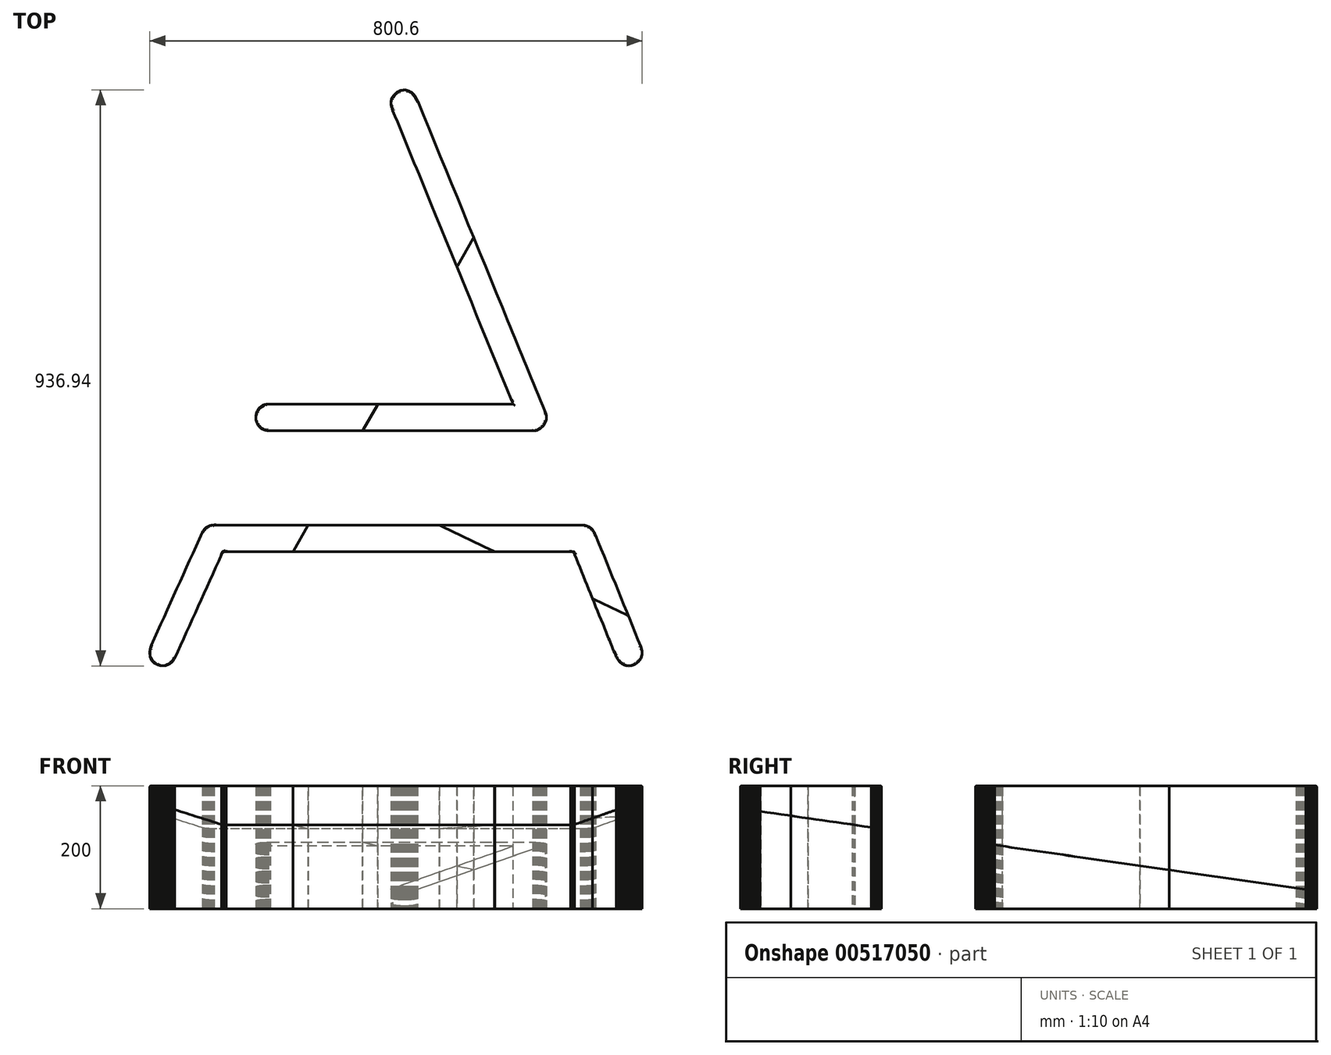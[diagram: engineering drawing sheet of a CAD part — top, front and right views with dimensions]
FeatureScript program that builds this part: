
annotation { "Feature Type Name" : "Feature", "Feature Type Description" : "" }
export const myFeature = defineFeature(function(context is Context, id is Id, definition is map)
    precondition{}
    {
        {
            var Q0;
            Q0=qCreatedBy(makeId("Top.planeOp"),FACE);
            var sketch = newSketch(context, id + "F0", { "sketchPlane" : qUnion([Q0])});
            skLineSegment(sketch, "E0", {"start": v(4.38, -239.2) * mm, "end": v(22.85, -239.2) * mm});
            skLineSegment(sketch, "E1", {"start": v(22.85, -239.2) * mm, "end": v(41.32, -239.2) * mm});
            skLineSegment(sketch, "E2", {"start": v(41.32, -239.2) * mm, "end": v(59.79, -239.2) * mm});
            skLineSegment(sketch, "E3", {"start": v(59.79, -239.2) * mm, "end": v(78.26, -239.2) * mm});
            skLineSegment(sketch, "E4", {"start": v(78.26, -239.2) * mm, "end": v(96.73, -239.2) * mm});
            skLineSegment(sketch, "E5", {"start": v(96.73, -239.2) * mm, "end": v(115.2, -239.2) * mm});
            skLineSegment(sketch, "E6", {"start": v(115.2, -239.2) * mm, "end": v(133.66, -239.2) * mm});
            skLineSegment(sketch, "E7", {"start": v(133.66, -239.2) * mm, "end": v(152.13, -239.2) * mm});
            skLineSegment(sketch, "E8", {"start": v(152.13, -239.2) * mm, "end": v(170.6, -239.2) * mm});
            skLineSegment(sketch, "E9", {"start": v(170.6, -239.2) * mm, "end": v(189.07, -239.2) * mm});
            skLineSegment(sketch, "E10", {"start": v(189.07, -239.2) * mm, "end": v(207.53, -239.2) * mm});
            skLineSegment(sketch, "E11", {"start": v(207.53, -239.2) * mm, "end": v(226, -239.2) * mm});
            skLineSegment(sketch, "E12", {"start": v(226, -239.2) * mm, "end": v(244.47, -239.2) * mm});
            skLineSegment(sketch, "E13", {"start": v(244.47, -239.2) * mm, "end": v(262.94, -239.2) * mm});
            skLineSegment(sketch, "E14", {"start": v(262.94, -239.2) * mm, "end": v(281.4, -239.2) * mm});
            skLineSegment(sketch, "E15", {"start": v(281.4, -239.2) * mm, "end": v(299.88, -239.2) * mm});
            skLineSegment(sketch, "E16", {"start": v(299.88, -239.2) * mm, "end": v(302.32, -239.25) * mm});
            skLineSegment(sketch, "E17", {"start": v(302.32, -239.25) * mm, "end": v(304.6, -239.4) * mm});
            skLineSegment(sketch, "E18", {"start": v(304.6, -239.4) * mm, "end": v(306.73, -239.65) * mm});
            skLineSegment(sketch, "E19", {"start": v(306.73, -239.65) * mm, "end": v(308.7, -240.02) * mm});
            skLineSegment(sketch, "E20", {"start": v(308.7, -240.02) * mm, "end": v(310.55, -240.51) * mm});
            skLineSegment(sketch, "E21", {"start": v(310.55, -240.51) * mm, "end": v(312.26, -241.13) * mm});
            skLineSegment(sketch, "E22", {"start": v(312.26, -241.13) * mm, "end": v(313.86, -241.89) * mm});
            skLineSegment(sketch, "E23", {"start": v(313.86, -241.89) * mm, "end": v(315.35, -242.78) * mm});
            skLineSegment(sketch, "E24", {"start": v(315.35, -242.78) * mm, "end": v(316.74, -243.83) * mm});
            skLineSegment(sketch, "E25", {"start": v(316.74, -243.83) * mm, "end": v(318.05, -245.03) * mm});
            skLineSegment(sketch, "E26", {"start": v(318.05, -245.03) * mm, "end": v(319.27, -246.39) * mm});
            skLineSegment(sketch, "E27", {"start": v(319.27, -246.39) * mm, "end": v(320.43, -247.92) * mm});
            skLineSegment(sketch, "E28", {"start": v(320.43, -247.92) * mm, "end": v(321.53, -249.63) * mm});
            skLineSegment(sketch, "E29", {"start": v(321.53, -249.63) * mm, "end": v(322.58, -251.52) * mm});
            skLineSegment(sketch, "E30", {"start": v(322.58, -251.52) * mm, "end": v(323.6, -253.6) * mm});
            skLineSegment(sketch, "E31", {"start": v(323.6, -253.6) * mm, "end": v(324.58, -255.88) * mm});
            skLineSegment(sketch, "E32", {"start": v(324.58, -255.88) * mm, "end": v(329.18, -267.18) * mm});
            skLineSegment(sketch, "E33", {"start": v(329.18, -267.18) * mm, "end": v(333.78, -278.48) * mm});
            skLineSegment(sketch, "E34", {"start": v(333.78, -278.48) * mm, "end": v(338.38, -289.78) * mm});
            skLineSegment(sketch, "E35", {"start": v(338.38, -289.78) * mm, "end": v(342.98, -301.08) * mm});
            skLineSegment(sketch, "E36", {"start": v(342.98, -301.08) * mm, "end": v(347.58, -312.38) * mm});
            skLineSegment(sketch, "E37", {"start": v(347.58, -312.38) * mm, "end": v(352.18, -323.68) * mm});
            skLineSegment(sketch, "E38", {"start": v(352.18, -323.68) * mm, "end": v(356.78, -334.98) * mm});
            skLineSegment(sketch, "E39", {"start": v(356.78, -334.98) * mm, "end": v(361.37, -346.29) * mm});
            skLineSegment(sketch, "E40", {"start": v(361.37, -346.29) * mm, "end": v(365.97, -357.59) * mm});
            skLineSegment(sketch, "E41", {"start": v(365.97, -357.59) * mm, "end": v(370.57, -368.89) * mm});
            skLineSegment(sketch, "E42", {"start": v(370.57, -368.89) * mm, "end": v(375.16, -380.19) * mm});
            skLineSegment(sketch, "E43", {"start": v(375.16, -380.19) * mm, "end": v(379.76, -391.5) * mm});
            skLineSegment(sketch, "E44", {"start": v(379.76, -391.5) * mm, "end": v(384.35, -402.8) * mm});
            skLineSegment(sketch, "E45", {"start": v(384.35, -402.8) * mm, "end": v(388.95, -414.1) * mm});
            skLineSegment(sketch, "E46", {"start": v(388.95, -414.1) * mm, "end": v(393.54, -425.4) * mm});
            skLineSegment(sketch, "E47", {"start": v(393.54, -425.4) * mm, "end": v(398.13, -436.7) * mm});
            skLineSegment(sketch, "E48", {"start": v(398.13, -436.7) * mm, "end": v(399, -439.11) * mm});
            skLineSegment(sketch, "E49", {"start": v(399, -439.11) * mm, "end": v(399.66, -441.5) * mm});
            skLineSegment(sketch, "E50", {"start": v(399.66, -441.5) * mm, "end": v(400.09, -443.83) * mm});
            skLineSegment(sketch, "E51", {"start": v(400.09, -443.83) * mm, "end": v(400.3, -446.11) * mm});
            skLineSegment(sketch, "E52", {"start": v(400.3, -446.11) * mm, "end": v(400.3, -448.34) * mm});
            skLineSegment(sketch, "E53", {"start": v(400.3, -448.34) * mm, "end": v(400.08, -450.5) * mm});
            skLineSegment(sketch, "E54", {"start": v(400.08, -450.5) * mm, "end": v(399.65, -452.58) * mm});
            skLineSegment(sketch, "E55", {"start": v(399.65, -452.58) * mm, "end": v(399.02, -454.58) * mm});
            skLineSegment(sketch, "E56", {"start": v(399.02, -454.58) * mm, "end": v(398.19, -456.5) * mm});
            skLineSegment(sketch, "E57", {"start": v(398.19, -456.5) * mm, "end": v(397.16, -458.3) * mm});
            skLineSegment(sketch, "E58", {"start": v(397.16, -458.3) * mm, "end": v(395.93, -460.01) * mm});
            skLineSegment(sketch, "E59", {"start": v(395.93, -460.01) * mm, "end": v(394.51, -461.6) * mm});
            skLineSegment(sketch, "E60", {"start": v(394.51, -461.6) * mm, "end": v(392.9, -463.08) * mm});
            skLineSegment(sketch, "E61", {"start": v(392.9, -463.08) * mm, "end": v(391.1, -464.41) * mm});
            skLineSegment(sketch, "E62", {"start": v(391.1, -464.41) * mm, "end": v(389.13, -465.61) * mm});
            skLineSegment(sketch, "E63", {"start": v(389.13, -465.61) * mm, "end": v(386.97, -466.67) * mm});
            skLineSegment(sketch, "E64", {"start": v(386.97, -466.67) * mm, "end": v(384.89, -467.45) * mm});
            skLineSegment(sketch, "E65", {"start": v(384.89, -467.45) * mm, "end": v(382.79, -468.02) * mm});
            skLineSegment(sketch, "E66", {"start": v(382.79, -468.02) * mm, "end": v(380.69, -468.35) * mm});
            skLineSegment(sketch, "E67", {"start": v(380.69, -468.35) * mm, "end": v(378.6, -468.47) * mm});
            skLineSegment(sketch, "E68", {"start": v(378.6, -468.47) * mm, "end": v(376.53, -468.36) * mm});
            skLineSegment(sketch, "E69", {"start": v(376.53, -468.36) * mm, "end": v(374.5, -468.05) * mm});
            skLineSegment(sketch, "E70", {"start": v(374.5, -468.05) * mm, "end": v(372.5, -467.52) * mm});
            skLineSegment(sketch, "E71", {"start": v(372.5, -467.52) * mm, "end": v(370.56, -466.79) * mm});
            skLineSegment(sketch, "E72", {"start": v(370.56, -466.79) * mm, "end": v(368.69, -465.85) * mm});
            skLineSegment(sketch, "E73", {"start": v(368.69, -465.85) * mm, "end": v(366.9, -464.71) * mm});
            skLineSegment(sketch, "E74", {"start": v(366.9, -464.71) * mm, "end": v(365.19, -463.38) * mm});
            skLineSegment(sketch, "E75", {"start": v(365.19, -463.38) * mm, "end": v(363.58, -461.85) * mm});
            skLineSegment(sketch, "E76", {"start": v(363.58, -461.85) * mm, "end": v(362.08, -460.13) * mm});
            skLineSegment(sketch, "E77", {"start": v(362.08, -460.13) * mm, "end": v(360.71, -458.23) * mm});
            skLineSegment(sketch, "E78", {"start": v(360.71, -458.23) * mm, "end": v(359.47, -456.14) * mm});
            skLineSegment(sketch, "E79", {"start": v(359.47, -456.14) * mm, "end": v(358.38, -453.87) * mm});
            skLineSegment(sketch, "E80", {"start": v(358.38, -453.87) * mm, "end": v(356.95, -450.55) * mm});
            skLineSegment(sketch, "E81", {"start": v(356.95, -450.55) * mm, "end": v(355.54, -447.22) * mm});
            skLineSegment(sketch, "E82", {"start": v(355.54, -447.22) * mm, "end": v(354.13, -443.88) * mm});
            skLineSegment(sketch, "E83", {"start": v(354.13, -443.88) * mm, "end": v(352.74, -440.54) * mm});
            skLineSegment(sketch, "E84", {"start": v(352.74, -440.54) * mm, "end": v(351.36, -437.2) * mm});
            skLineSegment(sketch, "E85", {"start": v(351.36, -437.2) * mm, "end": v(349.98, -433.85) * mm});
            skLineSegment(sketch, "E86", {"start": v(349.98, -433.85) * mm, "end": v(348.61, -430.5) * mm});
            skLineSegment(sketch, "E87", {"start": v(348.61, -430.5) * mm, "end": v(347.25, -427.14) * mm});
            skLineSegment(sketch, "E88", {"start": v(347.25, -427.14) * mm, "end": v(345.9, -423.79) * mm});
            skLineSegment(sketch, "E89", {"start": v(345.9, -423.79) * mm, "end": v(344.54, -420.43) * mm});
            skLineSegment(sketch, "E90", {"start": v(344.54, -420.43) * mm, "end": v(343.19, -417.07) * mm});
            skLineSegment(sketch, "E91", {"start": v(343.19, -417.07) * mm, "end": v(341.83, -413.71) * mm});
            skLineSegment(sketch, "E92", {"start": v(341.83, -413.71) * mm, "end": v(340.48, -410.36) * mm});
            skLineSegment(sketch, "E93", {"start": v(340.48, -410.36) * mm, "end": v(339.13, -407) * mm});
            skLineSegment(sketch, "E94", {"start": v(339.13, -407) * mm, "end": v(337.77, -403.64) * mm});
            skLineSegment(sketch, "E95", {"start": v(337.77, -403.64) * mm, "end": v(336.4, -400.29) * mm});
            skLineSegment(sketch, "E96", {"start": v(336.4, -400.29) * mm, "end": v(333.53, -393.2) * mm});
            skLineSegment(sketch, "E97", {"start": v(333.53, -393.2) * mm, "end": v(330.65, -386.13) * mm});
            skLineSegment(sketch, "E98", {"start": v(330.65, -386.13) * mm, "end": v(327.76, -379.05) * mm});
            skLineSegment(sketch, "E99", {"start": v(327.76, -379.05) * mm, "end": v(324.88, -371.96) * mm});
            skLineSegment(sketch, "E100", {"start": v(324.88, -371.96) * mm, "end": v(322, -364.88) * mm});
            skLineSegment(sketch, "E101", {"start": v(322, -364.88) * mm, "end": v(319.12, -357.8) * mm});
            skLineSegment(sketch, "E102", {"start": v(319.12, -357.8) * mm, "end": v(316.24, -350.72) * mm});
            skLineSegment(sketch, "E103", {"start": v(316.24, -350.72) * mm, "end": v(313.37, -343.63) * mm});
            skLineSegment(sketch, "E104", {"start": v(313.37, -343.63) * mm, "end": v(310.5, -336.55) * mm});
            skLineSegment(sketch, "E105", {"start": v(310.5, -336.55) * mm, "end": v(307.62, -329.47) * mm});
            skLineSegment(sketch, "E106", {"start": v(307.62, -329.47) * mm, "end": v(304.74, -322.38) * mm});
            skLineSegment(sketch, "E107", {"start": v(304.74, -322.38) * mm, "end": v(301.87, -315.3) * mm});
            skLineSegment(sketch, "E108", {"start": v(301.87, -315.3) * mm, "end": v(299, -308.2) * mm});
            skLineSegment(sketch, "E109", {"start": v(299, -308.2) * mm, "end": v(296.14, -301.12) * mm});
            skLineSegment(sketch, "E110", {"start": v(296.14, -301.12) * mm, "end": v(293.28, -294.03) * mm});
            skLineSegment(sketch, "E111", {"start": v(293.28, -294.03) * mm, "end": v(290.42, -286.94) * mm});
            skLineSegment(sketch, "E112", {"start": v(290.42, -286.94) * mm, "end": v(290.17, -286.36) * mm});
            skLineSegment(sketch, "E113", {"start": v(290.17, -286.36) * mm, "end": v(289.91, -285.82) * mm});
            skLineSegment(sketch, "E114", {"start": v(289.91, -285.82) * mm, "end": v(289.64, -285.32) * mm});
            skLineSegment(sketch, "E115", {"start": v(289.64, -285.32) * mm, "end": v(289.36, -284.87) * mm});
            skLineSegment(sketch, "E116", {"start": v(289.36, -284.87) * mm, "end": v(289.07, -284.46) * mm});
            skLineSegment(sketch, "E117", {"start": v(289.07, -284.46) * mm, "end": v(288.75, -284.1) * mm});
            skLineSegment(sketch, "E118", {"start": v(288.75, -284.1) * mm, "end": v(288.41, -283.77) * mm});
            skLineSegment(sketch, "E119", {"start": v(288.41, -283.77) * mm, "end": v(288.05, -283.48) * mm});
            skLineSegment(sketch, "E120", {"start": v(288.05, -283.48) * mm, "end": v(287.66, -283.23) * mm});
            skLineSegment(sketch, "E121", {"start": v(287.66, -283.23) * mm, "end": v(287.24, -283.02) * mm});
            skLineSegment(sketch, "E122", {"start": v(287.24, -283.02) * mm, "end": v(286.78, -282.84) * mm});
            skLineSegment(sketch, "E123", {"start": v(286.78, -282.84) * mm, "end": v(286.3, -282.7) * mm});
            skLineSegment(sketch, "E124", {"start": v(286.3, -282.7) * mm, "end": v(285.77, -282.6) * mm});
            skLineSegment(sketch, "E125", {"start": v(285.77, -282.6) * mm, "end": v(285.2, -282.51) * mm});
            skLineSegment(sketch, "E126", {"start": v(285.2, -282.51) * mm, "end": v(284.59, -282.47) * mm});
            skLineSegment(sketch, "E127", {"start": v(284.59, -282.47) * mm, "end": v(283.93, -282.46) * mm});
            skLineSegment(sketch, "E128", {"start": v(283.93, -282.46) * mm, "end": v(261.52, -282.47) * mm});
            skLineSegment(sketch, "E129", {"start": v(261.52, -282.47) * mm, "end": v(239.12, -282.48) * mm});
            skLineSegment(sketch, "E130", {"start": v(239.12, -282.48) * mm, "end": v(216.71, -282.48) * mm});
            skLineSegment(sketch, "E131", {"start": v(216.71, -282.48) * mm, "end": v(194.3, -282.49) * mm});
            skLineSegment(sketch, "E132", {"start": v(194.3, -282.49) * mm, "end": v(171.9, -282.49) * mm});
            skLineSegment(sketch, "E133", {"start": v(171.9, -282.49) * mm, "end": v(149.5, -282.49) * mm});
            skLineSegment(sketch, "E134", {"start": v(149.5, -282.49) * mm, "end": v(127.1, -282.49) * mm});
            skLineSegment(sketch, "E135", {"start": v(127.1, -282.49) * mm, "end": v(104.69, -282.48) * mm});
            skLineSegment(sketch, "E136", {"start": v(104.69, -282.48) * mm, "end": v(82.28, -282.48) * mm});
            skLineSegment(sketch, "E137", {"start": v(82.28, -282.48) * mm, "end": v(59.88, -282.47) * mm});
            skLineSegment(sketch, "E138", {"start": v(59.88, -282.47) * mm, "end": v(37.47, -282.47) * mm});
            skLineSegment(sketch, "E139", {"start": v(37.47, -282.47) * mm, "end": v(15.07, -282.46) * mm});
            skLineSegment(sketch, "E140", {"start": v(15.07, -282.46) * mm, "end": v(-7.34, -282.46) * mm});
            skLineSegment(sketch, "E141", {"start": v(-7.34, -282.46) * mm, "end": v(-29.74, -282.45) * mm});
            skLineSegment(sketch, "E142", {"start": v(-29.74, -282.45) * mm, "end": v(-52.15, -282.45) * mm});
            skLineSegment(sketch, "E143", {"start": v(-52.15, -282.45) * mm, "end": v(-74.56, -282.45) * mm});
            skLineSegment(sketch, "E144", {"start": v(-74.56, -282.45) * mm, "end": v(-87.15, -282.45) * mm});
            skLineSegment(sketch, "E145", {"start": v(-87.15, -282.45) * mm, "end": v(-99.74, -282.45) * mm});
            skLineSegment(sketch, "E146", {"start": v(-99.74, -282.45) * mm, "end": v(-112.33, -282.45) * mm});
            skLineSegment(sketch, "E147", {"start": v(-112.33, -282.45) * mm, "end": v(-124.93, -282.46) * mm});
            skLineSegment(sketch, "E148", {"start": v(-124.93, -282.46) * mm, "end": v(-137.52, -282.47) * mm});
            skLineSegment(sketch, "E149", {"start": v(-137.52, -282.47) * mm, "end": v(-150.11, -282.47) * mm});
            skLineSegment(sketch, "E150", {"start": v(-150.11, -282.47) * mm, "end": v(-162.7, -282.48) * mm});
            skLineSegment(sketch, "E151", {"start": v(-162.7, -282.48) * mm, "end": v(-175.3, -282.48) * mm});
            skLineSegment(sketch, "E152", {"start": v(-175.3, -282.48) * mm, "end": v(-187.9, -282.49) * mm});
            skLineSegment(sketch, "E153", {"start": v(-187.9, -282.49) * mm, "end": v(-200.49, -282.49) * mm});
            skLineSegment(sketch, "E154", {"start": v(-200.49, -282.49) * mm, "end": v(-213.08, -282.5) * mm});
            skLineSegment(sketch, "E155", {"start": v(-213.08, -282.5) * mm, "end": v(-225.67, -282.49) * mm});
            skLineSegment(sketch, "E156", {"start": v(-225.67, -282.49) * mm, "end": v(-238.26, -282.48) * mm});
            skLineSegment(sketch, "E157", {"start": v(-238.26, -282.48) * mm, "end": v(-250.86, -282.47) * mm});
            skLineSegment(sketch, "E158", {"start": v(-250.86, -282.47) * mm, "end": v(-263.45, -282.46) * mm});
            skLineSegment(sketch, "E159", {"start": v(-263.45, -282.46) * mm, "end": v(-276.04, -282.44) * mm});
            skLineSegment(sketch, "E160", {"start": v(-276.04, -282.44) * mm, "end": v(-276.75, -282.46) * mm});
            skLineSegment(sketch, "E161", {"start": v(-276.75, -282.46) * mm, "end": v(-277.42, -282.5) * mm});
            skLineSegment(sketch, "E162", {"start": v(-277.42, -282.5) * mm, "end": v(-278.05, -282.57) * mm});
            skLineSegment(sketch, "E163", {"start": v(-278.05, -282.57) * mm, "end": v(-278.63, -282.68) * mm});
            skLineSegment(sketch, "E164", {"start": v(-278.63, -282.68) * mm, "end": v(-279.18, -282.81) * mm});
            skLineSegment(sketch, "E165", {"start": v(-279.18, -282.81) * mm, "end": v(-279.7, -283) * mm});
            skLineSegment(sketch, "E166", {"start": v(-279.7, -283) * mm, "end": v(-280.17, -283.2) * mm});
            skLineSegment(sketch, "E167", {"start": v(-280.17, -283.2) * mm, "end": v(-280.62, -283.46) * mm});
            skLineSegment(sketch, "E168", {"start": v(-280.62, -283.46) * mm, "end": v(-281.05, -283.75) * mm});
            skLineSegment(sketch, "E169", {"start": v(-281.05, -283.75) * mm, "end": v(-281.45, -284.1) * mm});
            skLineSegment(sketch, "E170", {"start": v(-281.45, -284.1) * mm, "end": v(-281.83, -284.48) * mm});
            skLineSegment(sketch, "E171", {"start": v(-281.83, -284.48) * mm, "end": v(-282.18, -284.91) * mm});
            skLineSegment(sketch, "E172", {"start": v(-282.18, -284.91) * mm, "end": v(-282.53, -285.4) * mm});
            skLineSegment(sketch, "E173", {"start": v(-282.53, -285.4) * mm, "end": v(-282.85, -285.93) * mm});
            skLineSegment(sketch, "E174", {"start": v(-282.85, -285.93) * mm, "end": v(-283.17, -286.52) * mm});
            skLineSegment(sketch, "E175", {"start": v(-283.17, -286.52) * mm, "end": v(-283.48, -287.16) * mm});
            skLineSegment(sketch, "E176", {"start": v(-283.48, -287.16) * mm, "end": v(-288.23, -297.71) * mm});
            skLineSegment(sketch, "E177", {"start": v(-288.23, -297.71) * mm, "end": v(-293, -308.27) * mm});
            skLineSegment(sketch, "E178", {"start": v(-293, -308.27) * mm, "end": v(-297.76, -318.82) * mm});
            skLineSegment(sketch, "E179", {"start": v(-297.76, -318.82) * mm, "end": v(-302.52, -329.37) * mm});
            skLineSegment(sketch, "E180", {"start": v(-302.52, -329.37) * mm, "end": v(-307.3, -339.92) * mm});
            skLineSegment(sketch, "E181", {"start": v(-307.3, -339.92) * mm, "end": v(-312.06, -350.46) * mm});
            skLineSegment(sketch, "E182", {"start": v(-312.06, -350.46) * mm, "end": v(-316.84, -361.01) * mm});
            skLineSegment(sketch, "E183", {"start": v(-316.84, -361.01) * mm, "end": v(-321.61, -371.56) * mm});
            skLineSegment(sketch, "E184", {"start": v(-321.61, -371.56) * mm, "end": v(-326.39, -382.1) * mm});
            skLineSegment(sketch, "E185", {"start": v(-326.39, -382.1) * mm, "end": v(-331.17, -392.65) * mm});
            skLineSegment(sketch, "E186", {"start": v(-331.17, -392.65) * mm, "end": v(-335.95, -403.2) * mm});
            skLineSegment(sketch, "E187", {"start": v(-335.95, -403.2) * mm, "end": v(-340.73, -413.74) * mm});
            skLineSegment(sketch, "E188", {"start": v(-340.73, -413.74) * mm, "end": v(-345.5, -424.28) * mm});
            skLineSegment(sketch, "E189", {"start": v(-345.5, -424.28) * mm, "end": v(-350.29, -434.82) * mm});
            skLineSegment(sketch, "E190", {"start": v(-350.29, -434.82) * mm, "end": v(-355.07, -445.37) * mm});
            skLineSegment(sketch, "E191", {"start": v(-355.07, -445.37) * mm, "end": v(-359.85, -455.9) * mm});
            skLineSegment(sketch, "E192", {"start": v(-359.85, -455.9) * mm, "end": v(-360.64, -457.5) * mm});
            skLineSegment(sketch, "E193", {"start": v(-360.64, -457.5) * mm, "end": v(-361.53, -458.99) * mm});
            skLineSegment(sketch, "E194", {"start": v(-361.53, -458.99) * mm, "end": v(-362.51, -460.37) * mm});
            skLineSegment(sketch, "E195", {"start": v(-362.51, -460.37) * mm, "end": v(-363.58, -461.65) * mm});
            skLineSegment(sketch, "E196", {"start": v(-363.58, -461.65) * mm, "end": v(-364.73, -462.83) * mm});
            skLineSegment(sketch, "E197", {"start": v(-364.73, -462.83) * mm, "end": v(-365.96, -463.9) * mm});
            skLineSegment(sketch, "E198", {"start": v(-365.96, -463.9) * mm, "end": v(-367.26, -464.85) * mm});
            skLineSegment(sketch, "E199", {"start": v(-367.26, -464.85) * mm, "end": v(-368.64, -465.7) * mm});
            skLineSegment(sketch, "E200", {"start": v(-368.64, -465.7) * mm, "end": v(-370.09, -466.42) * mm});
            skLineSegment(sketch, "E201", {"start": v(-370.09, -466.42) * mm, "end": v(-371.6, -467.03) * mm});
            skLineSegment(sketch, "E202", {"start": v(-371.6, -467.03) * mm, "end": v(-373.17, -467.53) * mm});
            skLineSegment(sketch, "E203", {"start": v(-373.17, -467.53) * mm, "end": v(-374.8, -467.9) * mm});
            skLineSegment(sketch, "E204", {"start": v(-374.8, -467.9) * mm, "end": v(-376.47, -468.15) * mm});
            skLineSegment(sketch, "E205", {"start": v(-376.47, -468.15) * mm, "end": v(-378.2, -468.28) * mm});
            skLineSegment(sketch, "E206", {"start": v(-378.2, -468.28) * mm, "end": v(-379.96, -468.29) * mm});
            skLineSegment(sketch, "E207", {"start": v(-379.96, -468.29) * mm, "end": v(-381.77, -468.16) * mm});
            skLineSegment(sketch, "E208", {"start": v(-381.77, -468.16) * mm, "end": v(-383.48, -467.92) * mm});
            skLineSegment(sketch, "E209", {"start": v(-383.48, -467.92) * mm, "end": v(-385.15, -467.57) * mm});
            skLineSegment(sketch, "E210", {"start": v(-385.15, -467.57) * mm, "end": v(-386.78, -467.1) * mm});
            skLineSegment(sketch, "E211", {"start": v(-386.78, -467.1) * mm, "end": v(-388.34, -466.53) * mm});
            skLineSegment(sketch, "E212", {"start": v(-388.34, -466.53) * mm, "end": v(-389.84, -465.85) * mm});
            skLineSegment(sketch, "E213", {"start": v(-389.84, -465.85) * mm, "end": v(-391.27, -465.07) * mm});
            skLineSegment(sketch, "E214", {"start": v(-391.27, -465.07) * mm, "end": v(-392.63, -464.19) * mm});
            skLineSegment(sketch, "E215", {"start": v(-392.63, -464.19) * mm, "end": v(-393.89, -463.21) * mm});
            skLineSegment(sketch, "E216", {"start": v(-393.89, -463.21) * mm, "end": v(-395.06, -462.14) * mm});
            skLineSegment(sketch, "E217", {"start": v(-395.06, -462.14) * mm, "end": v(-396.13, -460.98) * mm});
            skLineSegment(sketch, "E218", {"start": v(-396.13, -460.98) * mm, "end": v(-397.08, -459.74) * mm});
            skLineSegment(sketch, "E219", {"start": v(-397.08, -459.74) * mm, "end": v(-397.92, -458.4) * mm});
            skLineSegment(sketch, "E220", {"start": v(-397.92, -458.4) * mm, "end": v(-398.64, -457) * mm});
            skLineSegment(sketch, "E221", {"start": v(-398.64, -457) * mm, "end": v(-399.22, -455.51) * mm});
            skLineSegment(sketch, "E222", {"start": v(-399.22, -455.51) * mm, "end": v(-399.66, -453.95) * mm});
            skLineSegment(sketch, "E223", {"start": v(-399.66, -453.95) * mm, "end": v(-399.96, -452.32) * mm});
            skLineSegment(sketch, "E224", {"start": v(-399.96, -452.32) * mm, "end": v(-400.08, -451.27) * mm});
            skLineSegment(sketch, "E225", {"start": v(-400.08, -451.27) * mm, "end": v(-400.18, -450.2) * mm});
            skLineSegment(sketch, "E226", {"start": v(-400.18, -450.2) * mm, "end": v(-400.25, -449.13) * mm});
            skLineSegment(sketch, "E227", {"start": v(-400.25, -449.13) * mm, "end": v(-400.29, -448.04) * mm});
            skLineSegment(sketch, "E228", {"start": v(-400.29, -448.04) * mm, "end": v(-400.3, -446.94) * mm});
            skLineSegment(sketch, "E229", {"start": v(-400.3, -446.94) * mm, "end": v(-400.28, -445.84) * mm});
            skLineSegment(sketch, "E230", {"start": v(-400.28, -445.84) * mm, "end": v(-400.22, -444.73) * mm});
            skLineSegment(sketch, "E231", {"start": v(-400.22, -444.73) * mm, "end": v(-400.14, -443.63) * mm});
            skLineSegment(sketch, "E232", {"start": v(-400.14, -443.63) * mm, "end": v(-400.02, -442.53) * mm});
            skLineSegment(sketch, "E233", {"start": v(-400.02, -442.53) * mm, "end": v(-399.86, -441.45) * mm});
            skLineSegment(sketch, "E234", {"start": v(-399.86, -441.45) * mm, "end": v(-399.67, -440.38) * mm});
            skLineSegment(sketch, "E235", {"start": v(-399.67, -440.38) * mm, "end": v(-399.43, -439.32) * mm});
            skLineSegment(sketch, "E236", {"start": v(-399.43, -439.32) * mm, "end": v(-399.16, -438.29) * mm});
            skLineSegment(sketch, "E237", {"start": v(-399.16, -438.29) * mm, "end": v(-398.85, -437.28) * mm});
            skLineSegment(sketch, "E238", {"start": v(-398.85, -437.28) * mm, "end": v(-398.5, -436.3) * mm});
            skLineSegment(sketch, "E239", {"start": v(-398.5, -436.3) * mm, "end": v(-398.1, -435.34) * mm});
            skLineSegment(sketch, "E240", {"start": v(-398.1, -435.34) * mm, "end": v(-392.92, -423.78) * mm});
            skLineSegment(sketch, "E241", {"start": v(-392.92, -423.78) * mm, "end": v(-387.74, -412.22) * mm});
            skLineSegment(sketch, "E242", {"start": v(-387.74, -412.22) * mm, "end": v(-382.54, -400.66) * mm});
            skLineSegment(sketch, "E243", {"start": v(-382.54, -400.66) * mm, "end": v(-377.34, -389.1) * mm});
            skLineSegment(sketch, "E244", {"start": v(-377.34, -389.1) * mm, "end": v(-372.13, -377.56) * mm});
            skLineSegment(sketch, "E245", {"start": v(-372.13, -377.56) * mm, "end": v(-366.91, -366.01) * mm});
            skLineSegment(sketch, "E246", {"start": v(-366.91, -366.01) * mm, "end": v(-361.69, -354.47) * mm});
            skLineSegment(sketch, "E247", {"start": v(-361.69, -354.47) * mm, "end": v(-356.46, -342.93) * mm});
            skLineSegment(sketch, "E248", {"start": v(-356.46, -342.93) * mm, "end": v(-351.23, -331.39) * mm});
            skLineSegment(sketch, "E249", {"start": v(-351.23, -331.39) * mm, "end": v(-346, -319.85) * mm});
            skLineSegment(sketch, "E250", {"start": v(-346, -319.85) * mm, "end": v(-340.76, -308.31) * mm});
            skLineSegment(sketch, "E251", {"start": v(-340.76, -308.31) * mm, "end": v(-335.52, -296.77) * mm});
            skLineSegment(sketch, "E252", {"start": v(-335.52, -296.77) * mm, "end": v(-330.28, -285.24) * mm});
            skLineSegment(sketch, "E253", {"start": v(-330.28, -285.24) * mm, "end": v(-325.04, -273.7) * mm});
            skLineSegment(sketch, "E254", {"start": v(-325.04, -273.7) * mm, "end": v(-319.8, -262.17) * mm});
            skLineSegment(sketch, "E255", {"start": v(-319.8, -262.17) * mm, "end": v(-314.56, -250.63) * mm});
            skLineSegment(sketch, "E256", {"start": v(-314.56, -250.63) * mm, "end": v(-313.9, -249.32) * mm});
            skLineSegment(sketch, "E257", {"start": v(-313.9, -249.32) * mm, "end": v(-313.2, -248.1) * mm});
            skLineSegment(sketch, "E258", {"start": v(-313.2, -248.1) * mm, "end": v(-312.43, -246.97) * mm});
            skLineSegment(sketch, "E259", {"start": v(-312.43, -246.97) * mm, "end": v(-311.6, -245.91) * mm});
            skLineSegment(sketch, "E260", {"start": v(-311.6, -245.91) * mm, "end": v(-310.72, -244.94) * mm});
            skLineSegment(sketch, "E261", {"start": v(-310.72, -244.94) * mm, "end": v(-309.78, -244.05) * mm});
            skLineSegment(sketch, "E262", {"start": v(-309.78, -244.05) * mm, "end": v(-308.79, -243.24) * mm});
            skLineSegment(sketch, "E263", {"start": v(-308.79, -243.24) * mm, "end": v(-307.74, -242.51) * mm});
            skLineSegment(sketch, "E264", {"start": v(-307.74, -242.51) * mm, "end": v(-306.64, -241.86) * mm});
            skLineSegment(sketch, "E265", {"start": v(-306.64, -241.86) * mm, "end": v(-305.49, -241.28) * mm});
            skLineSegment(sketch, "E266", {"start": v(-305.49, -241.28) * mm, "end": v(-304.29, -240.77) * mm});
            skLineSegment(sketch, "E267", {"start": v(-304.29, -240.77) * mm, "end": v(-303.04, -240.34) * mm});
            skLineSegment(sketch, "E268", {"start": v(-303.04, -240.34) * mm, "end": v(-301.74, -239.97) * mm});
            skLineSegment(sketch, "E269", {"start": v(-301.74, -239.97) * mm, "end": v(-300.4, -239.68) * mm});
            skLineSegment(sketch, "E270", {"start": v(-300.4, -239.68) * mm, "end": v(-299.03, -239.45) * mm});
            skLineSegment(sketch, "E271", {"start": v(-299.03, -239.45) * mm, "end": v(-297.6, -239.3) * mm});
            skLineSegment(sketch, "E272", {"start": v(-297.6, -239.3) * mm, "end": v(-297.2, -239.26) * mm});
            skLineSegment(sketch, "E273", {"start": v(-297.2, -239.26) * mm, "end": v(-296.8, -239.24) * mm});
            skLineSegment(sketch, "E274", {"start": v(-296.8, -239.24) * mm, "end": v(-296.4, -239.21) * mm});
            skLineSegment(sketch, "E275", {"start": v(-296.4, -239.21) * mm, "end": v(-295.99, -239.2) * mm});
            skLineSegment(sketch, "E276", {"start": v(-295.99, -239.2) * mm, "end": v(-295.58, -239.19) * mm});
            skLineSegment(sketch, "E277", {"start": v(-295.58, -239.19) * mm, "end": v(-295.17, -239.18) * mm});
            skLineSegment(sketch, "E278", {"start": v(-295.17, -239.18) * mm, "end": v(-294.77, -239.18) * mm});
            skLineSegment(sketch, "E279", {"start": v(-294.77, -239.18) * mm, "end": v(-294.36, -239.18) * mm});
            skLineSegment(sketch, "E280", {"start": v(-294.36, -239.18) * mm, "end": v(-293.95, -239.18) * mm});
            skLineSegment(sketch, "E281", {"start": v(-293.95, -239.18) * mm, "end": v(-293.55, -239.18) * mm});
            skLineSegment(sketch, "E282", {"start": v(-293.55, -239.18) * mm, "end": v(-293.14, -239.19) * mm});
            skLineSegment(sketch, "E283", {"start": v(-293.14, -239.19) * mm, "end": v(-292.73, -239.2) * mm});
            skLineSegment(sketch, "E284", {"start": v(-292.73, -239.2) * mm, "end": v(-292.33, -239.2) * mm});
            skLineSegment(sketch, "E285", {"start": v(-292.33, -239.2) * mm, "end": v(-291.92, -239.2) * mm});
            skLineSegment(sketch, "E286", {"start": v(-291.92, -239.2) * mm, "end": v(-291.51, -239.2) * mm});
            skLineSegment(sketch, "E287", {"start": v(-291.51, -239.2) * mm, "end": v(-291.1, -239.2) * mm});
            skLineSegment(sketch, "E288", {"start": v(-291.1, -239.2) * mm, "end": v(-272.64, -239.2) * mm});
            skLineSegment(sketch, "E289", {"start": v(-272.64, -239.2) * mm, "end": v(-254.17, -239.2) * mm});
            skLineSegment(sketch, "E290", {"start": v(-254.17, -239.2) * mm, "end": v(-235.7, -239.2) * mm});
            skLineSegment(sketch, "E291", {"start": v(-235.7, -239.2) * mm, "end": v(-217.23, -239.2) * mm});
            skLineSegment(sketch, "E292", {"start": v(-217.23, -239.2) * mm, "end": v(-198.77, -239.2) * mm});
            skLineSegment(sketch, "E293", {"start": v(-198.77, -239.2) * mm, "end": v(-180.3, -239.2) * mm});
            skLineSegment(sketch, "E294", {"start": v(-180.3, -239.2) * mm, "end": v(-161.83, -239.2) * mm});
            skLineSegment(sketch, "E295", {"start": v(-161.83, -239.2) * mm, "end": v(-143.36, -239.2) * mm});
            skLineSegment(sketch, "E296", {"start": v(-143.36, -239.2) * mm, "end": v(-124.9, -239.2) * mm});
            skLineSegment(sketch, "E297", {"start": v(-124.9, -239.2) * mm, "end": v(-106.43, -239.2) * mm});
            skLineSegment(sketch, "E298", {"start": v(-106.43, -239.2) * mm, "end": v(-87.96, -239.2) * mm});
            skLineSegment(sketch, "E299", {"start": v(-87.96, -239.2) * mm, "end": v(-69.49, -239.2) * mm});
            skLineSegment(sketch, "E300", {"start": v(-69.49, -239.2) * mm, "end": v(-51.02, -239.2) * mm});
            skLineSegment(sketch, "E301", {"start": v(-51.02, -239.2) * mm, "end": v(-32.55, -239.2) * mm});
            skLineSegment(sketch, "E302", {"start": v(-32.55, -239.2) * mm, "end": v(-14.08, -239.2) * mm});
            skLineSegment(sketch, "E303", {"start": v(-14.08, -239.2) * mm, "end": v(4.38, -239.2) * mm});
            skLineSegment(sketch, "E304", {"start": v(190.22, -42.46) * mm, "end": v(190.07, -42.05) * mm});
            skLineSegment(sketch, "E305", {"start": v(190.07, -42.05) * mm, "end": v(189.92, -41.65) * mm});
            skLineSegment(sketch, "E306", {"start": v(189.92, -41.65) * mm, "end": v(189.78, -41.26) * mm});
            skLineSegment(sketch, "E307", {"start": v(189.78, -41.26) * mm, "end": v(189.64, -40.88) * mm});
            skLineSegment(sketch, "E308", {"start": v(189.64, -40.88) * mm, "end": v(189.5, -40.51) * mm});
            skLineSegment(sketch, "E309", {"start": v(189.5, -40.51) * mm, "end": v(189.38, -40.15) * mm});
            skLineSegment(sketch, "E310", {"start": v(189.38, -40.15) * mm, "end": v(189.25, -39.8) * mm});
            skLineSegment(sketch, "E311", {"start": v(189.25, -39.8) * mm, "end": v(189.12, -39.46) * mm});
            skLineSegment(sketch, "E312", {"start": v(189.12, -39.46) * mm, "end": v(189, -39.12) * mm});
            skLineSegment(sketch, "E313", {"start": v(189, -39.12) * mm, "end": v(188.87, -38.79) * mm});
            skLineSegment(sketch, "E314", {"start": v(188.87, -38.79) * mm, "end": v(188.75, -38.46) * mm});
            skLineSegment(sketch, "E315", {"start": v(188.75, -38.46) * mm, "end": v(188.63, -38.14) * mm});
            skLineSegment(sketch, "E316", {"start": v(188.63, -38.14) * mm, "end": v(188.5, -37.82) * mm});
            skLineSegment(sketch, "E317", {"start": v(188.5, -37.82) * mm, "end": v(188.39, -37.5) * mm});
            skLineSegment(sketch, "E318", {"start": v(188.39, -37.5) * mm, "end": v(188.26, -37.2) * mm});
            skLineSegment(sketch, "E319", {"start": v(188.26, -37.2) * mm, "end": v(188.14, -36.88) * mm});
            skLineSegment(sketch, "E320", {"start": v(188.14, -36.88) * mm, "end": v(179.93, -16.85) * mm});
            skLineSegment(sketch, "E321", {"start": v(179.93, -16.85) * mm, "end": v(171.72, 3.2) * mm});
            skLineSegment(sketch, "E322", {"start": v(171.72, 3.2) * mm, "end": v(163.5, 23.23) * mm});
            skLineSegment(sketch, "E323", {"start": v(163.5, 23.23) * mm, "end": v(155.3, 43.27) * mm});
            skLineSegment(sketch, "E324", {"start": v(155.3, 43.27) * mm, "end": v(147.09, 63.3) * mm});
            skLineSegment(sketch, "E325", {"start": v(147.09, 63.3) * mm, "end": v(138.88, 83.34) * mm});
            skLineSegment(sketch, "E326", {"start": v(138.88, 83.34) * mm, "end": v(130.67, 103.38) * mm});
            skLineSegment(sketch, "E327", {"start": v(130.67, 103.38) * mm, "end": v(122.46, 123.42) * mm});
            skLineSegment(sketch, "E328", {"start": v(122.46, 123.42) * mm, "end": v(114.25, 143.45) * mm});
            skLineSegment(sketch, "E329", {"start": v(114.25, 143.45) * mm, "end": v(106.04, 163.5) * mm});
            skLineSegment(sketch, "E330", {"start": v(106.04, 163.5) * mm, "end": v(97.83, 183.53) * mm});
            skLineSegment(sketch, "E331", {"start": v(97.83, 183.53) * mm, "end": v(89.62, 203.57) * mm});
            skLineSegment(sketch, "E332", {"start": v(89.62, 203.57) * mm, "end": v(81.4, 223.6) * mm});
            skLineSegment(sketch, "E333", {"start": v(81.4, 223.6) * mm, "end": v(73.2, 243.64) * mm});
            skLineSegment(sketch, "E334", {"start": v(73.2, 243.64) * mm, "end": v(64.99, 263.68) * mm});
            skLineSegment(sketch, "E335", {"start": v(64.99, 263.68) * mm, "end": v(56.78, 283.72) * mm});
            skLineSegment(sketch, "E336", {"start": v(56.78, 283.72) * mm, "end": v(52.9, 293.19) * mm});
            skLineSegment(sketch, "E337", {"start": v(52.9, 293.19) * mm, "end": v(49.02, 302.66) * mm});
            skLineSegment(sketch, "E338", {"start": v(49.02, 302.66) * mm, "end": v(45.15, 312.13) * mm});
            skLineSegment(sketch, "E339", {"start": v(45.15, 312.13) * mm, "end": v(41.28, 321.6) * mm});
            skLineSegment(sketch, "E340", {"start": v(41.28, 321.6) * mm, "end": v(37.41, 331.07) * mm});
            skLineSegment(sketch, "E341", {"start": v(37.41, 331.07) * mm, "end": v(33.54, 340.55) * mm});
            skLineSegment(sketch, "E342", {"start": v(33.54, 340.55) * mm, "end": v(29.67, 350.02) * mm});
            skLineSegment(sketch, "E343", {"start": v(29.67, 350.02) * mm, "end": v(25.8, 359.5) * mm});
            skLineSegment(sketch, "E344", {"start": v(25.8, 359.5) * mm, "end": v(21.92, 368.96) * mm});
            skLineSegment(sketch, "E345", {"start": v(21.92, 368.96) * mm, "end": v(18.04, 378.43) * mm});
            skLineSegment(sketch, "E346", {"start": v(18.04, 378.43) * mm, "end": v(14.15, 387.9) * mm});
            skLineSegment(sketch, "E347", {"start": v(14.15, 387.9) * mm, "end": v(10.26, 397.36) * mm});
            skLineSegment(sketch, "E348", {"start": v(10.26, 397.36) * mm, "end": v(6.35, 406.81) * mm});
            skLineSegment(sketch, "E349", {"start": v(6.35, 406.81) * mm, "end": v(2.44, 416.27) * mm});
            skLineSegment(sketch, "E350", {"start": v(2.44, 416.27) * mm, "end": v(-1.48, 425.72) * mm});
            skLineSegment(sketch, "E351", {"start": v(-1.48, 425.72) * mm, "end": v(-5.41, 435.17) * mm});
            skLineSegment(sketch, "E352", {"start": v(-5.41, 435.17) * mm, "end": v(-6.4, 437.74) * mm});
            skLineSegment(sketch, "E353", {"start": v(-6.4, 437.74) * mm, "end": v(-7.16, 440.17) * mm});
            skLineSegment(sketch, "E354", {"start": v(-7.16, 440.17) * mm, "end": v(-7.7, 442.45) * mm});
            skLineSegment(sketch, "E355", {"start": v(-7.7, 442.45) * mm, "end": v(-8.06, 444.6) * mm});
            skLineSegment(sketch, "E356", {"start": v(-8.06, 444.6) * mm, "end": v(-8.22, 446.62) * mm});
            skLineSegment(sketch, "E357", {"start": v(-8.22, 446.62) * mm, "end": v(-8.2, 448.52) * mm});
            skLineSegment(sketch, "E358", {"start": v(-8.2, 448.52) * mm, "end": v(-8.02, 450.3) * mm});
            skLineSegment(sketch, "E359", {"start": v(-8.02, 450.3) * mm, "end": v(-7.68, 451.98) * mm});
            skLineSegment(sketch, "E360", {"start": v(-7.68, 451.98) * mm, "end": v(-7.21, 453.56) * mm});
            skLineSegment(sketch, "E361", {"start": v(-7.21, 453.56) * mm, "end": v(-6.62, 455.05) * mm});
            skLineSegment(sketch, "E362", {"start": v(-6.62, 455.05) * mm, "end": v(-5.9, 456.46) * mm});
            skLineSegment(sketch, "E363", {"start": v(-5.9, 456.46) * mm, "end": v(-5.1, 457.78) * mm});
            skLineSegment(sketch, "E364", {"start": v(-5.1, 457.78) * mm, "end": v(-4.2, 459.03) * mm});
            skLineSegment(sketch, "E365", {"start": v(-4.2, 459.03) * mm, "end": v(-3.22, 460.22) * mm});
            skLineSegment(sketch, "E366", {"start": v(-3.22, 460.22) * mm, "end": v(-2.18, 461.36) * mm});
            skLineSegment(sketch, "E367", {"start": v(-2.18, 461.36) * mm, "end": v(-1.1, 462.44) * mm});
            skLineSegment(sketch, "E368", {"start": v(-1.1, 462.44) * mm, "end": v(0.6, 463.9) * mm});
            skLineSegment(sketch, "E369", {"start": v(0.6, 463.9) * mm, "end": v(2.37, 465.17) * mm});
            skLineSegment(sketch, "E370", {"start": v(2.37, 465.17) * mm, "end": v(4.22, 466.23) * mm});
            skLineSegment(sketch, "E371", {"start": v(4.22, 466.23) * mm, "end": v(6.13, 467.09) * mm});
            skLineSegment(sketch, "E372", {"start": v(6.13, 467.09) * mm, "end": v(8.09, 467.74) * mm});
            skLineSegment(sketch, "E373", {"start": v(8.09, 467.74) * mm, "end": v(10.08, 468.18) * mm});
            skLineSegment(sketch, "E374", {"start": v(10.08, 468.18) * mm, "end": v(12.08, 468.43) * mm});
            skLineSegment(sketch, "E375", {"start": v(12.08, 468.43) * mm, "end": v(14.1, 468.47) * mm});
            skLineSegment(sketch, "E376", {"start": v(14.1, 468.47) * mm, "end": v(16.1, 468.3) * mm});
            skLineSegment(sketch, "E377", {"start": v(16.1, 468.3) * mm, "end": v(18.08, 467.93) * mm});
            skLineSegment(sketch, "E378", {"start": v(18.08, 467.93) * mm, "end": v(20.02, 467.36) * mm});
            skLineSegment(sketch, "E379", {"start": v(20.02, 467.36) * mm, "end": v(21.92, 466.58) * mm});
            skLineSegment(sketch, "E380", {"start": v(21.92, 466.58) * mm, "end": v(23.76, 465.6) * mm});
            skLineSegment(sketch, "E381", {"start": v(23.76, 465.6) * mm, "end": v(25.51, 464.41) * mm});
            skLineSegment(sketch, "E382", {"start": v(25.51, 464.41) * mm, "end": v(27.18, 463.02) * mm});
            skLineSegment(sketch, "E383", {"start": v(27.18, 463.02) * mm, "end": v(28.75, 461.43) * mm});
            skLineSegment(sketch, "E384", {"start": v(28.75, 461.43) * mm, "end": v(29.28, 460.8) * mm});
            skLineSegment(sketch, "E385", {"start": v(29.28, 460.8) * mm, "end": v(29.8, 460.16) * mm});
            skLineSegment(sketch, "E386", {"start": v(29.8, 460.16) * mm, "end": v(30.31, 459.5) * mm});
            skLineSegment(sketch, "E387", {"start": v(30.31, 459.5) * mm, "end": v(30.8, 458.83) * mm});
            skLineSegment(sketch, "E388", {"start": v(30.8, 458.83) * mm, "end": v(31.28, 458.14) * mm});
            skLineSegment(sketch, "E389", {"start": v(31.28, 458.14) * mm, "end": v(31.74, 457.43) * mm});
            skLineSegment(sketch, "E390", {"start": v(31.74, 457.43) * mm, "end": v(32.18, 456.72) * mm});
            skLineSegment(sketch, "E391", {"start": v(32.18, 456.72) * mm, "end": v(32.61, 456) * mm});
            skLineSegment(sketch, "E392", {"start": v(32.61, 456) * mm, "end": v(33.03, 455.25) * mm});
            skLineSegment(sketch, "E393", {"start": v(33.03, 455.25) * mm, "end": v(33.43, 454.5) * mm});
            skLineSegment(sketch, "E394", {"start": v(33.43, 454.5) * mm, "end": v(33.82, 453.76) * mm});
            skLineSegment(sketch, "E395", {"start": v(33.82, 453.76) * mm, "end": v(34.2, 453) * mm});
            skLineSegment(sketch, "E396", {"start": v(34.2, 453) * mm, "end": v(34.56, 452.24) * mm});
            skLineSegment(sketch, "E397", {"start": v(34.56, 452.24) * mm, "end": v(34.9, 451.48) * mm});
            skLineSegment(sketch, "E398", {"start": v(34.9, 451.48) * mm, "end": v(35.24, 450.7) * mm});
            skLineSegment(sketch, "E399", {"start": v(35.24, 450.7) * mm, "end": v(35.56, 449.94) * mm});
            skLineSegment(sketch, "E400", {"start": v(35.56, 449.94) * mm, "end": v(44.72, 427.63) * mm});
            skLineSegment(sketch, "E401", {"start": v(44.72, 427.63) * mm, "end": v(53.87, 405.32) * mm});
            skLineSegment(sketch, "E402", {"start": v(53.87, 405.32) * mm, "end": v(63.03, 383) * mm});
            skLineSegment(sketch, "E403", {"start": v(63.03, 383) * mm, "end": v(72.18, 360.69) * mm});
            skLineSegment(sketch, "E404", {"start": v(72.18, 360.69) * mm, "end": v(81.33, 338.37) * mm});
            skLineSegment(sketch, "E405", {"start": v(81.33, 338.37) * mm, "end": v(90.48, 316.06) * mm});
            skLineSegment(sketch, "E406", {"start": v(90.48, 316.06) * mm, "end": v(99.63, 293.74) * mm});
            skLineSegment(sketch, "E407", {"start": v(99.63, 293.74) * mm, "end": v(108.78, 271.43) * mm});
            skLineSegment(sketch, "E408", {"start": v(108.78, 271.43) * mm, "end": v(117.92, 249.1) * mm});
            skLineSegment(sketch, "E409", {"start": v(117.92, 249.1) * mm, "end": v(127.07, 226.79) * mm});
            skLineSegment(sketch, "E410", {"start": v(127.07, 226.79) * mm, "end": v(136.21, 204.47) * mm});
            skLineSegment(sketch, "E411", {"start": v(136.21, 204.47) * mm, "end": v(145.36, 182.15) * mm});
            skLineSegment(sketch, "E412", {"start": v(145.36, 182.15) * mm, "end": v(154.5, 159.83) * mm});
            skLineSegment(sketch, "E413", {"start": v(154.5, 159.83) * mm, "end": v(163.64, 137.52) * mm});
            skLineSegment(sketch, "E414", {"start": v(163.64, 137.52) * mm, "end": v(172.79, 115.2) * mm});
            skLineSegment(sketch, "E415", {"start": v(172.79, 115.2) * mm, "end": v(181.93, 92.88) * mm});
            skLineSegment(sketch, "E416", {"start": v(181.93, 92.88) * mm, "end": v(185.72, 83.61) * mm});
            skLineSegment(sketch, "E417", {"start": v(185.72, 83.61) * mm, "end": v(189.5, 74.34) * mm});
            skLineSegment(sketch, "E418", {"start": v(189.5, 74.34) * mm, "end": v(193.29, 65.07) * mm});
            skLineSegment(sketch, "E419", {"start": v(193.29, 65.07) * mm, "end": v(197.06, 55.8) * mm});
            skLineSegment(sketch, "E420", {"start": v(197.06, 55.8) * mm, "end": v(200.84, 46.52) * mm});
            skLineSegment(sketch, "E421", {"start": v(200.84, 46.52) * mm, "end": v(204.62, 37.24) * mm});
            skLineSegment(sketch, "E422", {"start": v(204.62, 37.24) * mm, "end": v(208.4, 27.97) * mm});
            skLineSegment(sketch, "E423", {"start": v(208.4, 27.97) * mm, "end": v(212.18, 18.7) * mm});
            skLineSegment(sketch, "E424", {"start": v(212.18, 18.7) * mm, "end": v(215.97, 9.43) * mm});
            skLineSegment(sketch, "E425", {"start": v(215.97, 9.43) * mm, "end": v(219.77, 0.17) * mm});
            skLineSegment(sketch, "E426", {"start": v(219.77, 0.17) * mm, "end": v(223.58, -9.1) * mm});
            skLineSegment(sketch, "E427", {"start": v(223.58, -9.1) * mm, "end": v(227.4, -18.35) * mm});
            skLineSegment(sketch, "E428", {"start": v(227.4, -18.35) * mm, "end": v(231.23, -27.6) * mm});
            skLineSegment(sketch, "E429", {"start": v(231.23, -27.6) * mm, "end": v(235.08, -36.85) * mm});
            skLineSegment(sketch, "E430", {"start": v(235.08, -36.85) * mm, "end": v(238.94, -46.09) * mm});
            skLineSegment(sketch, "E431", {"start": v(238.94, -46.09) * mm, "end": v(242.82, -55.32) * mm});
            skLineSegment(sketch, "E432", {"start": v(242.82, -55.32) * mm, "end": v(243.94, -58.51) * mm});
            skLineSegment(sketch, "E433", {"start": v(243.94, -58.51) * mm, "end": v(244.57, -61.61) * mm});
            skLineSegment(sketch, "E434", {"start": v(244.57, -61.61) * mm, "end": v(244.75, -64.6) * mm});
            skLineSegment(sketch, "E435", {"start": v(244.75, -64.6) * mm, "end": v(244.52, -67.46) * mm});
            skLineSegment(sketch, "E436", {"start": v(244.52, -67.46) * mm, "end": v(243.91, -70.18) * mm});
            skLineSegment(sketch, "E437", {"start": v(243.91, -70.18) * mm, "end": v(242.96, -72.74) * mm});
            skLineSegment(sketch, "E438", {"start": v(242.96, -72.74) * mm, "end": v(241.71, -75.12) * mm});
            skLineSegment(sketch, "E439", {"start": v(241.71, -75.12) * mm, "end": v(240.19, -77.32) * mm});
            skLineSegment(sketch, "E440", {"start": v(240.19, -77.32) * mm, "end": v(238.43, -79.3) * mm});
            skLineSegment(sketch, "E441", {"start": v(238.43, -79.3) * mm, "end": v(236.47, -81.07) * mm});
            skLineSegment(sketch, "E442", {"start": v(236.47, -81.07) * mm, "end": v(234.36, -82.6) * mm});
            skLineSegment(sketch, "E443", {"start": v(234.36, -82.6) * mm, "end": v(232.1, -83.88) * mm});
            skLineSegment(sketch, "E444", {"start": v(232.1, -83.88) * mm, "end": v(229.77, -84.89) * mm});
            skLineSegment(sketch, "E445", {"start": v(229.77, -84.89) * mm, "end": v(227.37, -85.61) * mm});
            skLineSegment(sketch, "E446", {"start": v(227.37, -85.61) * mm, "end": v(224.96, -86.04) * mm});
            skLineSegment(sketch, "E447", {"start": v(224.96, -86.04) * mm, "end": v(222.56, -86.15) * mm});
            skLineSegment(sketch, "E448", {"start": v(222.56, -86.15) * mm, "end": v(222.4, -86.14) * mm});
            skLineSegment(sketch, "E449", {"start": v(222.4, -86.14) * mm, "end": v(222.24, -86.14) * mm});
            skLineSegment(sketch, "E450", {"start": v(222.24, -86.14) * mm, "end": v(222.09, -86.14) * mm});
            skLineSegment(sketch, "E451", {"start": v(222.09, -86.14) * mm, "end": v(221.93, -86.14) * mm});
            skLineSegment(sketch, "E452", {"start": v(221.93, -86.14) * mm, "end": v(221.77, -86.14) * mm});
            skLineSegment(sketch, "E453", {"start": v(221.77, -86.14) * mm, "end": v(221.62, -86.14) * mm});
            skLineSegment(sketch, "E454", {"start": v(221.62, -86.14) * mm, "end": v(221.46, -86.14) * mm});
            skLineSegment(sketch, "E455", {"start": v(221.46, -86.14) * mm, "end": v(221.3, -86.14) * mm});
            skLineSegment(sketch, "E456", {"start": v(221.3, -86.14) * mm, "end": v(221.15, -86.14) * mm});
            skLineSegment(sketch, "E457", {"start": v(221.15, -86.14) * mm, "end": v(221, -86.14) * mm});
            skLineSegment(sketch, "E458", {"start": v(221, -86.14) * mm, "end": v(220.84, -86.14) * mm});
            skLineSegment(sketch, "E459", {"start": v(220.84, -86.14) * mm, "end": v(220.68, -86.15) * mm});
            skLineSegment(sketch, "E460", {"start": v(220.68, -86.15) * mm, "end": v(220.52, -86.15) * mm});
            skLineSegment(sketch, "E461", {"start": v(220.52, -86.15) * mm, "end": v(220.37, -86.15) * mm});
            skLineSegment(sketch, "E462", {"start": v(220.37, -86.15) * mm, "end": v(220.21, -86.15) * mm});
            skLineSegment(sketch, "E463", {"start": v(220.21, -86.15) * mm, "end": v(220.06, -86.15) * mm});
            skLineSegment(sketch, "E464", {"start": v(220.06, -86.15) * mm, "end": v(193.53, -86.15) * mm});
            skLineSegment(sketch, "E465", {"start": v(193.53, -86.15) * mm, "end": v(167, -86.15) * mm});
            skLineSegment(sketch, "E466", {"start": v(167, -86.15) * mm, "end": v(140.47, -86.15) * mm});
            skLineSegment(sketch, "E467", {"start": v(140.47, -86.15) * mm, "end": v(113.95, -86.15) * mm});
            skLineSegment(sketch, "E468", {"start": v(113.95, -86.15) * mm, "end": v(87.42, -86.15) * mm});
            skLineSegment(sketch, "E469", {"start": v(87.42, -86.15) * mm, "end": v(60.9, -86.15) * mm});
            skLineSegment(sketch, "E470", {"start": v(60.9, -86.15) * mm, "end": v(34.36, -86.15) * mm});
            skLineSegment(sketch, "E471", {"start": v(34.36, -86.15) * mm, "end": v(7.84, -86.14) * mm});
            skLineSegment(sketch, "E472", {"start": v(7.84, -86.14) * mm, "end": v(-18.7, -86.14) * mm});
            skLineSegment(sketch, "E473", {"start": v(-18.7, -86.14) * mm, "end": v(-45.22, -86.13) * mm});
            skLineSegment(sketch, "E474", {"start": v(-45.22, -86.13) * mm, "end": v(-71.75, -86.12) * mm});
            skLineSegment(sketch, "E475", {"start": v(-71.75, -86.12) * mm, "end": v(-98.27, -86.1) * mm});
            skLineSegment(sketch, "E476", {"start": v(-98.27, -86.1) * mm, "end": v(-124.8, -86.1) * mm});
            skLineSegment(sketch, "E477", {"start": v(-124.8, -86.1) * mm, "end": v(-151.33, -86.08) * mm});
            skLineSegment(sketch, "E478", {"start": v(-151.33, -86.08) * mm, "end": v(-177.86, -86.06) * mm});
            skLineSegment(sketch, "E479", {"start": v(-177.86, -86.06) * mm, "end": v(-204.38, -86.03) * mm});
            skLineSegment(sketch, "E480", {"start": v(-204.38, -86.03) * mm, "end": v(-205.23, -86.02) * mm});
            skLineSegment(sketch, "E481", {"start": v(-205.23, -86.02) * mm, "end": v(-206.09, -85.99) * mm});
            skLineSegment(sketch, "E482", {"start": v(-206.09, -85.99) * mm, "end": v(-206.95, -85.93) * mm});
            skLineSegment(sketch, "E483", {"start": v(-206.95, -85.93) * mm, "end": v(-207.82, -85.86) * mm});
            skLineSegment(sketch, "E484", {"start": v(-207.82, -85.86) * mm, "end": v(-208.69, -85.76) * mm});
            skLineSegment(sketch, "E485", {"start": v(-208.69, -85.76) * mm, "end": v(-209.55, -85.64) * mm});
            skLineSegment(sketch, "E486", {"start": v(-209.55, -85.64) * mm, "end": v(-210.42, -85.5) * mm});
            skLineSegment(sketch, "E487", {"start": v(-210.42, -85.5) * mm, "end": v(-211.28, -85.33) * mm});
            skLineSegment(sketch, "E488", {"start": v(-211.28, -85.33) * mm, "end": v(-212.14, -85.14) * mm});
            skLineSegment(sketch, "E489", {"start": v(-212.14, -85.14) * mm, "end": v(-212.99, -84.93) * mm});
            skLineSegment(sketch, "E490", {"start": v(-212.99, -84.93) * mm, "end": v(-213.82, -84.7) * mm});
            skLineSegment(sketch, "E491", {"start": v(-213.82, -84.7) * mm, "end": v(-214.65, -84.43) * mm});
            skLineSegment(sketch, "E492", {"start": v(-214.65, -84.43) * mm, "end": v(-215.46, -84.15) * mm});
            skLineSegment(sketch, "E493", {"start": v(-215.46, -84.15) * mm, "end": v(-216.26, -83.84) * mm});
            skLineSegment(sketch, "E494", {"start": v(-216.26, -83.84) * mm, "end": v(-217.04, -83.51) * mm});
            skLineSegment(sketch, "E495", {"start": v(-217.04, -83.51) * mm, "end": v(-217.8, -83.16) * mm});
            skLineSegment(sketch, "E496", {"start": v(-217.8, -83.16) * mm, "end": v(-219.21, -82.37) * mm});
            skLineSegment(sketch, "E497", {"start": v(-219.21, -82.37) * mm, "end": v(-220.53, -81.43) * mm});
            skLineSegment(sketch, "E498", {"start": v(-220.53, -81.43) * mm, "end": v(-221.74, -80.36) * mm});
            skLineSegment(sketch, "E499", {"start": v(-221.74, -80.36) * mm, "end": v(-222.85, -79.16) * mm});
            skLineSegment(sketch, "E500", {"start": v(-222.85, -79.16) * mm, "end": v(-223.86, -77.84) * mm});
            skLineSegment(sketch, "E501", {"start": v(-223.86, -77.84) * mm, "end": v(-224.76, -76.43) * mm});
            skLineSegment(sketch, "E502", {"start": v(-224.76, -76.43) * mm, "end": v(-225.56, -74.93) * mm});
            skLineSegment(sketch, "E503", {"start": v(-225.56, -74.93) * mm, "end": v(-226.24, -73.35) * mm});
            skLineSegment(sketch, "E504", {"start": v(-226.24, -73.35) * mm, "end": v(-226.8, -71.7) * mm});
            skLineSegment(sketch, "E505", {"start": v(-226.8, -71.7) * mm, "end": v(-227.25, -70) * mm});
            skLineSegment(sketch, "E506", {"start": v(-227.25, -70) * mm, "end": v(-227.58, -68.25) * mm});
            skLineSegment(sketch, "E507", {"start": v(-227.58, -68.25) * mm, "end": v(-227.78, -66.48) * mm});
            skLineSegment(sketch, "E508", {"start": v(-227.78, -66.48) * mm, "end": v(-227.86, -64.69) * mm});
            skLineSegment(sketch, "E509", {"start": v(-227.86, -64.69) * mm, "end": v(-227.8, -62.88) * mm});
            skLineSegment(sketch, "E510", {"start": v(-227.8, -62.88) * mm, "end": v(-227.63, -61.09) * mm});
            skLineSegment(sketch, "E511", {"start": v(-227.63, -61.09) * mm, "end": v(-227.31, -59.3) * mm});
            skLineSegment(sketch, "E512", {"start": v(-227.31, -59.3) * mm, "end": v(-226.86, -57.5) * mm});
            skLineSegment(sketch, "E513", {"start": v(-226.86, -57.5) * mm, "end": v(-226.3, -55.8) * mm});
            skLineSegment(sketch, "E514", {"start": v(-226.3, -55.8) * mm, "end": v(-225.63, -54.18) * mm});
            skLineSegment(sketch, "E515", {"start": v(-225.63, -54.18) * mm, "end": v(-224.87, -52.65) * mm});
            skLineSegment(sketch, "E516", {"start": v(-224.87, -52.65) * mm, "end": v(-224, -51.23) * mm});
            skLineSegment(sketch, "E517", {"start": v(-224, -51.23) * mm, "end": v(-223.05, -49.9) * mm});
            skLineSegment(sketch, "E518", {"start": v(-223.05, -49.9) * mm, "end": v(-222, -48.67) * mm});
            skLineSegment(sketch, "E519", {"start": v(-222, -48.67) * mm, "end": v(-220.86, -47.54) * mm});
            skLineSegment(sketch, "E520", {"start": v(-220.86, -47.54) * mm, "end": v(-219.62, -46.52) * mm});
            skLineSegment(sketch, "E521", {"start": v(-219.62, -46.52) * mm, "end": v(-218.3, -45.61) * mm});
            skLineSegment(sketch, "E522", {"start": v(-218.3, -45.61) * mm, "end": v(-216.9, -44.81) * mm});
            skLineSegment(sketch, "E523", {"start": v(-216.9, -44.81) * mm, "end": v(-215.43, -44.13) * mm});
            skLineSegment(sketch, "E524", {"start": v(-215.43, -44.13) * mm, "end": v(-213.87, -43.56) * mm});
            skLineSegment(sketch, "E525", {"start": v(-213.87, -43.56) * mm, "end": v(-212.24, -43.1) * mm});
            skLineSegment(sketch, "E526", {"start": v(-212.24, -43.1) * mm, "end": v(-210.53, -42.78) * mm});
            skLineSegment(sketch, "E527", {"start": v(-210.53, -42.78) * mm, "end": v(-208.76, -42.57) * mm});
            skLineSegment(sketch, "E528", {"start": v(-208.76, -42.57) * mm, "end": v(-208.35, -42.54) * mm});
            skLineSegment(sketch, "E529", {"start": v(-208.35, -42.54) * mm, "end": v(-207.95, -42.52) * mm});
            skLineSegment(sketch, "E530", {"start": v(-207.95, -42.52) * mm, "end": v(-207.54, -42.5) * mm});
            skLineSegment(sketch, "E531", {"start": v(-207.54, -42.5) * mm, "end": v(-207.14, -42.49) * mm});
            skLineSegment(sketch, "E532", {"start": v(-207.14, -42.49) * mm, "end": v(-206.73, -42.48) * mm});
            skLineSegment(sketch, "E533", {"start": v(-206.73, -42.48) * mm, "end": v(-206.32, -42.47) * mm});
            skLineSegment(sketch, "E534", {"start": v(-206.32, -42.47) * mm, "end": v(-205.92, -42.47) * mm});
            skLineSegment(sketch, "E535", {"start": v(-205.92, -42.47) * mm, "end": v(-205.51, -42.47) * mm});
            skLineSegment(sketch, "E536", {"start": v(-205.51, -42.47) * mm, "end": v(-205.1, -42.47) * mm});
            skLineSegment(sketch, "E537", {"start": v(-205.1, -42.47) * mm, "end": v(-204.7, -42.47) * mm});
            skLineSegment(sketch, "E538", {"start": v(-204.7, -42.47) * mm, "end": v(-204.3, -42.48) * mm});
            skLineSegment(sketch, "E539", {"start": v(-204.3, -42.48) * mm, "end": v(-203.89, -42.48) * mm});
            skLineSegment(sketch, "E540", {"start": v(-203.89, -42.48) * mm, "end": v(-203.48, -42.48) * mm});
            skLineSegment(sketch, "E541", {"start": v(-203.48, -42.48) * mm, "end": v(-203.07, -42.49) * mm});
            skLineSegment(sketch, "E542", {"start": v(-203.07, -42.49) * mm, "end": v(-202.67, -42.49) * mm});
            skLineSegment(sketch, "E543", {"start": v(-202.67, -42.49) * mm, "end": v(-202.26, -42.49) * mm});
            skLineSegment(sketch, "E544", {"start": v(-202.26, -42.49) * mm, "end": v(-178.14, -42.49) * mm});
            skLineSegment(sketch, "E545", {"start": v(-178.14, -42.49) * mm, "end": v(-154.02, -42.49) * mm});
            skLineSegment(sketch, "E546", {"start": v(-154.02, -42.49) * mm, "end": v(-129.9, -42.48) * mm});
            skLineSegment(sketch, "E547", {"start": v(-129.9, -42.48) * mm, "end": v(-105.77, -42.48) * mm});
            skLineSegment(sketch, "E548", {"start": v(-105.77, -42.48) * mm, "end": v(-81.65, -42.48) * mm});
            skLineSegment(sketch, "E549", {"start": v(-81.65, -42.48) * mm, "end": v(-57.53, -42.48) * mm});
            skLineSegment(sketch, "E550", {"start": v(-57.53, -42.48) * mm, "end": v(-33.4, -42.48) * mm});
            skLineSegment(sketch, "E551", {"start": v(-33.4, -42.48) * mm, "end": v(-9.29, -42.47) * mm});
            skLineSegment(sketch, "E552", {"start": v(-9.29, -42.47) * mm, "end": v(14.83, -42.47) * mm});
            skLineSegment(sketch, "E553", {"start": v(14.83, -42.47) * mm, "end": v(38.96, -42.47) * mm});
            skLineSegment(sketch, "E554", {"start": v(38.96, -42.47) * mm, "end": v(63.08, -42.47) * mm});
            skLineSegment(sketch, "E555", {"start": v(63.08, -42.47) * mm, "end": v(87.2, -42.47) * mm});
            skLineSegment(sketch, "E556", {"start": v(87.2, -42.47) * mm, "end": v(111.32, -42.47) * mm});
            skLineSegment(sketch, "E557", {"start": v(111.32, -42.47) * mm, "end": v(135.44, -42.46) * mm});
            skLineSegment(sketch, "E558", {"start": v(135.44, -42.46) * mm, "end": v(159.56, -42.46) * mm});
            skLineSegment(sketch, "E559", {"start": v(159.56, -42.46) * mm, "end": v(183.69, -42.46) * mm});
            skLineSegment(sketch, "E560", {"start": v(183.69, -42.46) * mm, "end": v(184.06, -42.46) * mm});
            skLineSegment(sketch, "E561", {"start": v(184.06, -42.46) * mm, "end": v(184.43, -42.46) * mm});
            skLineSegment(sketch, "E562", {"start": v(184.43, -42.46) * mm, "end": v(184.8, -42.46) * mm});
            skLineSegment(sketch, "E563", {"start": v(184.8, -42.46) * mm, "end": v(185.17, -42.46) * mm});
            skLineSegment(sketch, "E564", {"start": v(185.17, -42.46) * mm, "end": v(185.55, -42.46) * mm});
            skLineSegment(sketch, "E565", {"start": v(185.55, -42.46) * mm, "end": v(185.94, -42.46) * mm});
            skLineSegment(sketch, "E566", {"start": v(185.94, -42.46) * mm, "end": v(186.32, -42.46) * mm});
            skLineSegment(sketch, "E567", {"start": v(186.32, -42.46) * mm, "end": v(186.72, -42.46) * mm});
            skLineSegment(sketch, "E568", {"start": v(186.72, -42.46) * mm, "end": v(187.12, -42.46) * mm});
            skLineSegment(sketch, "E569", {"start": v(187.12, -42.46) * mm, "end": v(187.53, -42.46) * mm});
            skLineSegment(sketch, "E570", {"start": v(187.53, -42.46) * mm, "end": v(187.95, -42.46) * mm});
            skLineSegment(sketch, "E571", {"start": v(187.95, -42.46) * mm, "end": v(188.38, -42.46) * mm});
            skLineSegment(sketch, "E572", {"start": v(188.38, -42.46) * mm, "end": v(188.82, -42.46) * mm});
            skLineSegment(sketch, "E573", {"start": v(188.82, -42.46) * mm, "end": v(189.28, -42.46) * mm});
            skLineSegment(sketch, "E574", {"start": v(189.28, -42.46) * mm, "end": v(189.74, -42.46) * mm});
            skLineSegment(sketch, "E575", {"start": v(189.74, -42.46) * mm, "end": v(190.22, -42.46) * mm});
            skSolve(sketch);
        }
        {
            var Q0;
            Q0 = qSketchRegion(id + "F0", true);
            extrude(context, id + "F1", {"entities" : qUnion([Q0]), "depth" : 200 * mm, "offsetDistance" : 25 * mm});
        }
        {
            var Q0;
            Q0=qCreatedBy(makeId("Right.planeOp"),FACE);
            var sketch = newSketch(context, id + "F2", { "sketchPlane" : qUnion([Q0])});
            skLineSegment(sketch, "E576", {"start": v(-618.73, 184.44) * mm, "end": v(668.12, 0) * mm});
            skLineSegment(sketch, "E577", {"start": v(-618.73, 184.44) * mm, "end": v(-618.73, 184.44) * mm});
            skLineSegment(sketch, "E578", {"start": v(668.12, 0) * mm, "end": v(668.12, 0) * mm});
            skSolve(sketch);
        }
        {
            var Q0;
            Q0 = qSketchRegion(id + "F2", true);
            extrude(context, id + "F3", {"entities" : qUnion([Q0]), "operationType" : NewBodyOperationType.REMOVE, "oppositeDirection" : true, "depth" : 592 * mm, "offsetDistance" : 25 * mm, "hasSecondDirection" : true, "secondDirectionOppositeDirection" : false, "secondDirectionDepth" : 675 * mm});
        }
        {
            var Q0;
            Q0=makeQuery(id+"F1.opExtrude","CAP_FACE",FACE,{"disambiguationData":[OSD([sQuery(id+"F0.wireOp",EDGE,"E0"),sQuery(id+"F0.wireOp",EDGE,"E1"),sQuery(id+"F0.wireOp",EDGE,"E2"),sQuery(id+"F0.wireOp",EDGE,"E3"),sQuery(id+"F0.wireOp",EDGE,"E4"),sQuery(id+"F0.wireOp",EDGE,"E5"),sQuery(id+"F0.wireOp",EDGE,"E6"),sQuery(id+"F0.wireOp",EDGE,"E7"),sQuery(id+"F0.wireOp",EDGE,"E8"),sQuery(id+"F0.wireOp",EDGE,"E9"),sQuery(id+"F0.wireOp",EDGE,"E10"),sQuery(id+"F0.wireOp",EDGE,"E11"),sQuery(id+"F0.wireOp",EDGE,"E12"),sQuery(id+"F0.wireOp",EDGE,"E13"),sQuery(id+"F0.wireOp",EDGE,"E14"),sQuery(id+"F0.wireOp",EDGE,"E15"),sQuery(id+"F0.wireOp",EDGE,"E16"),sQuery(id+"F0.wireOp",EDGE,"E17"),sQuery(id+"F0.wireOp",EDGE,"E18"),sQuery(id+"F0.wireOp",EDGE,"E19"),sQuery(id+"F0.wireOp",EDGE,"E20"),sQuery(id+"F0.wireOp",EDGE,"E21"),sQuery(id+"F0.wireOp",EDGE,"E22"),sQuery(id+"F0.wireOp",EDGE,"E23"),sQuery(id+"F0.wireOp",EDGE,"E24"),sQuery(id+"F0.wireOp",EDGE,"E25"),sQuery(id+"F0.wireOp",EDGE,"E26"),sQuery(id+"F0.wireOp",EDGE,"E27"),sQuery(id+"F0.wireOp",EDGE,"E28"),sQuery(id+"F0.wireOp",EDGE,"E29"),sQuery(id+"F0.wireOp",EDGE,"E30"),sQuery(id+"F0.wireOp",EDGE,"E31"),sQuery(id+"F0.wireOp",EDGE,"E32"),sQuery(id+"F0.wireOp",EDGE,"E33"),sQuery(id+"F0.wireOp",EDGE,"E34"),sQuery(id+"F0.wireOp",EDGE,"E35"),sQuery(id+"F0.wireOp",EDGE,"E36"),sQuery(id+"F0.wireOp",EDGE,"E37"),sQuery(id+"F0.wireOp",EDGE,"E38"),sQuery(id+"F0.wireOp",EDGE,"E39"),sQuery(id+"F0.wireOp",EDGE,"E40"),sQuery(id+"F0.wireOp",EDGE,"E41"),sQuery(id+"F0.wireOp",EDGE,"E42"),sQuery(id+"F0.wireOp",EDGE,"E43"),sQuery(id+"F0.wireOp",EDGE,"E44"),sQuery(id+"F0.wireOp",EDGE,"E45"),sQuery(id+"F0.wireOp",EDGE,"E46"),sQuery(id+"F0.wireOp",EDGE,"E47"),sQuery(id+"F0.wireOp",EDGE,"E48"),sQuery(id+"F0.wireOp",EDGE,"E49"),sQuery(id+"F0.wireOp",EDGE,"E50"),sQuery(id+"F0.wireOp",EDGE,"E51"),sQuery(id+"F0.wireOp",EDGE,"E52"),sQuery(id+"F0.wireOp",EDGE,"E53"),sQuery(id+"F0.wireOp",EDGE,"E54"),sQuery(id+"F0.wireOp",EDGE,"E55"),sQuery(id+"F0.wireOp",EDGE,"E56"),sQuery(id+"F0.wireOp",EDGE,"E57"),sQuery(id+"F0.wireOp",EDGE,"E58"),sQuery(id+"F0.wireOp",EDGE,"E59"),sQuery(id+"F0.wireOp",EDGE,"E60"),sQuery(id+"F0.wireOp",EDGE,"E61"),sQuery(id+"F0.wireOp",EDGE,"E62"),sQuery(id+"F0.wireOp",EDGE,"E63"),sQuery(id+"F0.wireOp",EDGE,"E64"),sQuery(id+"F0.wireOp",EDGE,"E65"),sQuery(id+"F0.wireOp",EDGE,"E66"),sQuery(id+"F0.wireOp",EDGE,"E67"),sQuery(id+"F0.wireOp",EDGE,"E68"),sQuery(id+"F0.wireOp",EDGE,"E69"),sQuery(id+"F0.wireOp",EDGE,"E70"),sQuery(id+"F0.wireOp",EDGE,"E71"),sQuery(id+"F0.wireOp",EDGE,"E72"),sQuery(id+"F0.wireOp",EDGE,"E73"),sQuery(id+"F0.wireOp",EDGE,"E74"),sQuery(id+"F0.wireOp",EDGE,"E75"),sQuery(id+"F0.wireOp",EDGE,"E76"),sQuery(id+"F0.wireOp",EDGE,"E77"),sQuery(id+"F0.wireOp",EDGE,"E78"),sQuery(id+"F0.wireOp",EDGE,"E79"),sQuery(id+"F0.wireOp",EDGE,"E80"),sQuery(id+"F0.wireOp",EDGE,"E81"),sQuery(id+"F0.wireOp",EDGE,"E82"),sQuery(id+"F0.wireOp",EDGE,"E83"),sQuery(id+"F0.wireOp",EDGE,"E84"),sQuery(id+"F0.wireOp",EDGE,"E85"),sQuery(id+"F0.wireOp",EDGE,"E86"),sQuery(id+"F0.wireOp",EDGE,"E87"),sQuery(id+"F0.wireOp",EDGE,"E88"),sQuery(id+"F0.wireOp",EDGE,"E89"),sQuery(id+"F0.wireOp",EDGE,"E90"),sQuery(id+"F0.wireOp",EDGE,"E91"),sQuery(id+"F0.wireOp",EDGE,"E92"),sQuery(id+"F0.wireOp",EDGE,"E93"),sQuery(id+"F0.wireOp",EDGE,"E94"),sQuery(id+"F0.wireOp",EDGE,"E95"),sQuery(id+"F0.wireOp",EDGE,"E96"),sQuery(id+"F0.wireOp",EDGE,"E97"),sQuery(id+"F0.wireOp",EDGE,"E98"),sQuery(id+"F0.wireOp",EDGE,"E99"),sQuery(id+"F0.wireOp",EDGE,"E100"),sQuery(id+"F0.wireOp",EDGE,"E101"),sQuery(id+"F0.wireOp",EDGE,"E102"),sQuery(id+"F0.wireOp",EDGE,"E103"),sQuery(id+"F0.wireOp",EDGE,"E104"),sQuery(id+"F0.wireOp",EDGE,"E105"),sQuery(id+"F0.wireOp",EDGE,"E106"),sQuery(id+"F0.wireOp",EDGE,"E107"),sQuery(id+"F0.wireOp",EDGE,"E108"),sQuery(id+"F0.wireOp",EDGE,"E109"),sQuery(id+"F0.wireOp",EDGE,"E110"),sQuery(id+"F0.wireOp",EDGE,"E111"),sQuery(id+"F0.wireOp",EDGE,"E112"),sQuery(id+"F0.wireOp",EDGE,"E113"),sQuery(id+"F0.wireOp",EDGE,"E114"),sQuery(id+"F0.wireOp",EDGE,"E115"),sQuery(id+"F0.wireOp",EDGE,"E116"),sQuery(id+"F0.wireOp",EDGE,"E117"),sQuery(id+"F0.wireOp",EDGE,"E118"),sQuery(id+"F0.wireOp",EDGE,"E119"),sQuery(id+"F0.wireOp",EDGE,"E120"),sQuery(id+"F0.wireOp",EDGE,"E121"),sQuery(id+"F0.wireOp",EDGE,"E122"),sQuery(id+"F0.wireOp",EDGE,"E123"),sQuery(id+"F0.wireOp",EDGE,"E124"),sQuery(id+"F0.wireOp",EDGE,"E125"),sQuery(id+"F0.wireOp",EDGE,"E126"),sQuery(id+"F0.wireOp",EDGE,"E127"),sQuery(id+"F0.wireOp",EDGE,"E128"),sQuery(id+"F0.wireOp",EDGE,"E129"),sQuery(id+"F0.wireOp",EDGE,"E130"),sQuery(id+"F0.wireOp",EDGE,"E131"),sQuery(id+"F0.wireOp",EDGE,"E132"),sQuery(id+"F0.wireOp",EDGE,"E133"),sQuery(id+"F0.wireOp",EDGE,"E134"),sQuery(id+"F0.wireOp",EDGE,"E135"),sQuery(id+"F0.wireOp",EDGE,"E136"),sQuery(id+"F0.wireOp",EDGE,"E137"),sQuery(id+"F0.wireOp",EDGE,"E138"),sQuery(id+"F0.wireOp",EDGE,"E139"),sQuery(id+"F0.wireOp",EDGE,"E140"),sQuery(id+"F0.wireOp",EDGE,"E141"),sQuery(id+"F0.wireOp",EDGE,"E142"),sQuery(id+"F0.wireOp",EDGE,"E143"),sQuery(id+"F0.wireOp",EDGE,"E144"),sQuery(id+"F0.wireOp",EDGE,"E145"),sQuery(id+"F0.wireOp",EDGE,"E146"),sQuery(id+"F0.wireOp",EDGE,"E147"),sQuery(id+"F0.wireOp",EDGE,"E148"),sQuery(id+"F0.wireOp",EDGE,"E149"),sQuery(id+"F0.wireOp",EDGE,"E150"),sQuery(id+"F0.wireOp",EDGE,"E151"),sQuery(id+"F0.wireOp",EDGE,"E152"),sQuery(id+"F0.wireOp",EDGE,"E153"),sQuery(id+"F0.wireOp",EDGE,"E154"),sQuery(id+"F0.wireOp",EDGE,"E155"),sQuery(id+"F0.wireOp",EDGE,"E156"),sQuery(id+"F0.wireOp",EDGE,"E157"),sQuery(id+"F0.wireOp",EDGE,"E158"),sQuery(id+"F0.wireOp",EDGE,"E159"),sQuery(id+"F0.wireOp",EDGE,"E160"),sQuery(id+"F0.wireOp",EDGE,"E161"),sQuery(id+"F0.wireOp",EDGE,"E162"),sQuery(id+"F0.wireOp",EDGE,"E163"),sQuery(id+"F0.wireOp",EDGE,"E164"),sQuery(id+"F0.wireOp",EDGE,"E165"),sQuery(id+"F0.wireOp",EDGE,"E166"),sQuery(id+"F0.wireOp",EDGE,"E167"),sQuery(id+"F0.wireOp",EDGE,"E168"),sQuery(id+"F0.wireOp",EDGE,"E169"),sQuery(id+"F0.wireOp",EDGE,"E170"),sQuery(id+"F0.wireOp",EDGE,"E171"),sQuery(id+"F0.wireOp",EDGE,"E172"),sQuery(id+"F0.wireOp",EDGE,"E173"),sQuery(id+"F0.wireOp",EDGE,"E174"),sQuery(id+"F0.wireOp",EDGE,"E175"),sQuery(id+"F0.wireOp",EDGE,"E176"),sQuery(id+"F0.wireOp",EDGE,"E177"),sQuery(id+"F0.wireOp",EDGE,"E178"),sQuery(id+"F0.wireOp",EDGE,"E179"),sQuery(id+"F0.wireOp",EDGE,"E180"),sQuery(id+"F0.wireOp",EDGE,"E181"),sQuery(id+"F0.wireOp",EDGE,"E182"),sQuery(id+"F0.wireOp",EDGE,"E183"),sQuery(id+"F0.wireOp",EDGE,"E184"),sQuery(id+"F0.wireOp",EDGE,"E185"),sQuery(id+"F0.wireOp",EDGE,"E186"),sQuery(id+"F0.wireOp",EDGE,"E187"),sQuery(id+"F0.wireOp",EDGE,"E188"),sQuery(id+"F0.wireOp",EDGE,"E189"),sQuery(id+"F0.wireOp",EDGE,"E190"),sQuery(id+"F0.wireOp",EDGE,"E191"),sQuery(id+"F0.wireOp",EDGE,"E192"),sQuery(id+"F0.wireOp",EDGE,"E193"),sQuery(id+"F0.wireOp",EDGE,"E194"),sQuery(id+"F0.wireOp",EDGE,"E195"),sQuery(id+"F0.wireOp",EDGE,"E196"),sQuery(id+"F0.wireOp",EDGE,"E197"),sQuery(id+"F0.wireOp",EDGE,"E198"),sQuery(id+"F0.wireOp",EDGE,"E199"),sQuery(id+"F0.wireOp",EDGE,"E200"),sQuery(id+"F0.wireOp",EDGE,"E201"),sQuery(id+"F0.wireOp",EDGE,"E202"),sQuery(id+"F0.wireOp",EDGE,"E203"),sQuery(id+"F0.wireOp",EDGE,"E204"),sQuery(id+"F0.wireOp",EDGE,"E205"),sQuery(id+"F0.wireOp",EDGE,"E206"),sQuery(id+"F0.wireOp",EDGE,"E207"),sQuery(id+"F0.wireOp",EDGE,"E208"),sQuery(id+"F0.wireOp",EDGE,"E209"),sQuery(id+"F0.wireOp",EDGE,"E210"),sQuery(id+"F0.wireOp",EDGE,"E211"),sQuery(id+"F0.wireOp",EDGE,"E212"),sQuery(id+"F0.wireOp",EDGE,"E213"),sQuery(id+"F0.wireOp",EDGE,"E214"),sQuery(id+"F0.wireOp",EDGE,"E215"),sQuery(id+"F0.wireOp",EDGE,"E216"),sQuery(id+"F0.wireOp",EDGE,"E217"),sQuery(id+"F0.wireOp",EDGE,"E218"),sQuery(id+"F0.wireOp",EDGE,"E219"),sQuery(id+"F0.wireOp",EDGE,"E220"),sQuery(id+"F0.wireOp",EDGE,"E221"),sQuery(id+"F0.wireOp",EDGE,"E222"),sQuery(id+"F0.wireOp",EDGE,"E223"),sQuery(id+"F0.wireOp",EDGE,"E224"),sQuery(id+"F0.wireOp",EDGE,"E225"),sQuery(id+"F0.wireOp",EDGE,"E226"),sQuery(id+"F0.wireOp",EDGE,"E227"),sQuery(id+"F0.wireOp",EDGE,"E228"),sQuery(id+"F0.wireOp",EDGE,"E229"),sQuery(id+"F0.wireOp",EDGE,"E230"),sQuery(id+"F0.wireOp",EDGE,"E231"),sQuery(id+"F0.wireOp",EDGE,"E232"),sQuery(id+"F0.wireOp",EDGE,"E233"),sQuery(id+"F0.wireOp",EDGE,"E234"),sQuery(id+"F0.wireOp",EDGE,"E235"),sQuery(id+"F0.wireOp",EDGE,"E236"),sQuery(id+"F0.wireOp",EDGE,"E237"),sQuery(id+"F0.wireOp",EDGE,"E238"),sQuery(id+"F0.wireOp",EDGE,"E239"),sQuery(id+"F0.wireOp",EDGE,"E240"),sQuery(id+"F0.wireOp",EDGE,"E241"),sQuery(id+"F0.wireOp",EDGE,"E242"),sQuery(id+"F0.wireOp",EDGE,"E243"),sQuery(id+"F0.wireOp",EDGE,"E244"),sQuery(id+"F0.wireOp",EDGE,"E245"),sQuery(id+"F0.wireOp",EDGE,"E246"),sQuery(id+"F0.wireOp",EDGE,"E247"),sQuery(id+"F0.wireOp",EDGE,"E248"),sQuery(id+"F0.wireOp",EDGE,"E249"),sQuery(id+"F0.wireOp",EDGE,"E250"),sQuery(id+"F0.wireOp",EDGE,"E251"),sQuery(id+"F0.wireOp",EDGE,"E252"),sQuery(id+"F0.wireOp",EDGE,"E253"),sQuery(id+"F0.wireOp",EDGE,"E254"),sQuery(id+"F0.wireOp",EDGE,"E255"),sQuery(id+"F0.wireOp",EDGE,"E256"),sQuery(id+"F0.wireOp",EDGE,"E257"),sQuery(id+"F0.wireOp",EDGE,"E258"),sQuery(id+"F0.wireOp",EDGE,"E259"),sQuery(id+"F0.wireOp",EDGE,"E260"),sQuery(id+"F0.wireOp",EDGE,"E261"),sQuery(id+"F0.wireOp",EDGE,"E262"),sQuery(id+"F0.wireOp",EDGE,"E263"),sQuery(id+"F0.wireOp",EDGE,"E264"),sQuery(id+"F0.wireOp",EDGE,"E265"),sQuery(id+"F0.wireOp",EDGE,"E266"),sQuery(id+"F0.wireOp",EDGE,"E267"),sQuery(id+"F0.wireOp",EDGE,"E268"),sQuery(id+"F0.wireOp",EDGE,"E269"),sQuery(id+"F0.wireOp",EDGE,"E270"),sQuery(id+"F0.wireOp",EDGE,"E271"),sQuery(id+"F0.wireOp",EDGE,"E272"),sQuery(id+"F0.wireOp",EDGE,"E273"),sQuery(id+"F0.wireOp",EDGE,"E274"),sQuery(id+"F0.wireOp",EDGE,"E275"),sQuery(id+"F0.wireOp",EDGE,"E276"),sQuery(id+"F0.wireOp",EDGE,"E277"),sQuery(id+"F0.wireOp",EDGE,"E278"),sQuery(id+"F0.wireOp",EDGE,"E279"),sQuery(id+"F0.wireOp",EDGE,"E280"),sQuery(id+"F0.wireOp",EDGE,"E281"),sQuery(id+"F0.wireOp",EDGE,"E282"),sQuery(id+"F0.wireOp",EDGE,"E283"),sQuery(id+"F0.wireOp",EDGE,"E284"),sQuery(id+"F0.wireOp",EDGE,"E285"),sQuery(id+"F0.wireOp",EDGE,"E286"),sQuery(id+"F0.wireOp",EDGE,"E287"),sQuery(id+"F0.wireOp",EDGE,"E288"),sQuery(id+"F0.wireOp",EDGE,"E289"),sQuery(id+"F0.wireOp",EDGE,"E290"),sQuery(id+"F0.wireOp",EDGE,"E291"),sQuery(id+"F0.wireOp",EDGE,"E292"),sQuery(id+"F0.wireOp",EDGE,"E293"),sQuery(id+"F0.wireOp",EDGE,"E294"),sQuery(id+"F0.wireOp",EDGE,"E295"),sQuery(id+"F0.wireOp",EDGE,"E296"),sQuery(id+"F0.wireOp",EDGE,"E297"),sQuery(id+"F0.wireOp",EDGE,"E298"),sQuery(id+"F0.wireOp",EDGE,"E299"),sQuery(id+"F0.wireOp",EDGE,"E300"),sQuery(id+"F0.wireOp",EDGE,"E301"),sQuery(id+"F0.wireOp",EDGE,"E302"),sQuery(id+"F0.wireOp",EDGE,"E303")])],"isStart":false});
            var Q1;
            Q1=makeQuery(id+"F1.opExtrude","CAP_FACE",FACE,{"disambiguationData":[OSD([sQuery(id+"F0.wireOp",EDGE,"E304"),sQuery(id+"F0.wireOp",EDGE,"E305"),sQuery(id+"F0.wireOp",EDGE,"E306"),sQuery(id+"F0.wireOp",EDGE,"E307"),sQuery(id+"F0.wireOp",EDGE,"E308"),sQuery(id+"F0.wireOp",EDGE,"E309"),sQuery(id+"F0.wireOp",EDGE,"E310"),sQuery(id+"F0.wireOp",EDGE,"E311"),sQuery(id+"F0.wireOp",EDGE,"E312"),sQuery(id+"F0.wireOp",EDGE,"E313"),sQuery(id+"F0.wireOp",EDGE,"E314"),sQuery(id+"F0.wireOp",EDGE,"E315"),sQuery(id+"F0.wireOp",EDGE,"E316"),sQuery(id+"F0.wireOp",EDGE,"E317"),sQuery(id+"F0.wireOp",EDGE,"E318"),sQuery(id+"F0.wireOp",EDGE,"E319"),sQuery(id+"F0.wireOp",EDGE,"E320"),sQuery(id+"F0.wireOp",EDGE,"E321"),sQuery(id+"F0.wireOp",EDGE,"E322"),sQuery(id+"F0.wireOp",EDGE,"E323"),sQuery(id+"F0.wireOp",EDGE,"E324"),sQuery(id+"F0.wireOp",EDGE,"E325"),sQuery(id+"F0.wireOp",EDGE,"E326"),sQuery(id+"F0.wireOp",EDGE,"E327"),sQuery(id+"F0.wireOp",EDGE,"E328"),sQuery(id+"F0.wireOp",EDGE,"E329"),sQuery(id+"F0.wireOp",EDGE,"E330"),sQuery(id+"F0.wireOp",EDGE,"E331"),sQuery(id+"F0.wireOp",EDGE,"E332"),sQuery(id+"F0.wireOp",EDGE,"E333"),sQuery(id+"F0.wireOp",EDGE,"E334"),sQuery(id+"F0.wireOp",EDGE,"E335"),sQuery(id+"F0.wireOp",EDGE,"E336"),sQuery(id+"F0.wireOp",EDGE,"E337"),sQuery(id+"F0.wireOp",EDGE,"E338"),sQuery(id+"F0.wireOp",EDGE,"E339"),sQuery(id+"F0.wireOp",EDGE,"E340"),sQuery(id+"F0.wireOp",EDGE,"E341"),sQuery(id+"F0.wireOp",EDGE,"E342"),sQuery(id+"F0.wireOp",EDGE,"E343"),sQuery(id+"F0.wireOp",EDGE,"E344"),sQuery(id+"F0.wireOp",EDGE,"E345"),sQuery(id+"F0.wireOp",EDGE,"E346"),sQuery(id+"F0.wireOp",EDGE,"E347"),sQuery(id+"F0.wireOp",EDGE,"E348"),sQuery(id+"F0.wireOp",EDGE,"E349"),sQuery(id+"F0.wireOp",EDGE,"E350"),sQuery(id+"F0.wireOp",EDGE,"E351"),sQuery(id+"F0.wireOp",EDGE,"E352"),sQuery(id+"F0.wireOp",EDGE,"E353"),sQuery(id+"F0.wireOp",EDGE,"E354"),sQuery(id+"F0.wireOp",EDGE,"E355"),sQuery(id+"F0.wireOp",EDGE,"E356"),sQuery(id+"F0.wireOp",EDGE,"E357"),sQuery(id+"F0.wireOp",EDGE,"E358"),sQuery(id+"F0.wireOp",EDGE,"E359"),sQuery(id+"F0.wireOp",EDGE,"E360"),sQuery(id+"F0.wireOp",EDGE,"E361"),sQuery(id+"F0.wireOp",EDGE,"E362"),sQuery(id+"F0.wireOp",EDGE,"E363"),sQuery(id+"F0.wireOp",EDGE,"E364"),sQuery(id+"F0.wireOp",EDGE,"E365"),sQuery(id+"F0.wireOp",EDGE,"E366"),sQuery(id+"F0.wireOp",EDGE,"E367"),sQuery(id+"F0.wireOp",EDGE,"E368"),sQuery(id+"F0.wireOp",EDGE,"E369"),sQuery(id+"F0.wireOp",EDGE,"E370"),sQuery(id+"F0.wireOp",EDGE,"E371"),sQuery(id+"F0.wireOp",EDGE,"E372"),sQuery(id+"F0.wireOp",EDGE,"E373"),sQuery(id+"F0.wireOp",EDGE,"E374"),sQuery(id+"F0.wireOp",EDGE,"E375"),sQuery(id+"F0.wireOp",EDGE,"E376"),sQuery(id+"F0.wireOp",EDGE,"E377"),sQuery(id+"F0.wireOp",EDGE,"E378"),sQuery(id+"F0.wireOp",EDGE,"E379"),sQuery(id+"F0.wireOp",EDGE,"E380"),sQuery(id+"F0.wireOp",EDGE,"E381"),sQuery(id+"F0.wireOp",EDGE,"E382"),sQuery(id+"F0.wireOp",EDGE,"E383"),sQuery(id+"F0.wireOp",EDGE,"E384"),sQuery(id+"F0.wireOp",EDGE,"E385"),sQuery(id+"F0.wireOp",EDGE,"E386"),sQuery(id+"F0.wireOp",EDGE,"E387"),sQuery(id+"F0.wireOp",EDGE,"E388"),sQuery(id+"F0.wireOp",EDGE,"E389"),sQuery(id+"F0.wireOp",EDGE,"E390"),sQuery(id+"F0.wireOp",EDGE,"E391"),sQuery(id+"F0.wireOp",EDGE,"E392"),sQuery(id+"F0.wireOp",EDGE,"E393"),sQuery(id+"F0.wireOp",EDGE,"E394"),sQuery(id+"F0.wireOp",EDGE,"E395"),sQuery(id+"F0.wireOp",EDGE,"E396"),sQuery(id+"F0.wireOp",EDGE,"E397"),sQuery(id+"F0.wireOp",EDGE,"E398"),sQuery(id+"F0.wireOp",EDGE,"E399"),sQuery(id+"F0.wireOp",EDGE,"E400"),sQuery(id+"F0.wireOp",EDGE,"E401"),sQuery(id+"F0.wireOp",EDGE,"E402"),sQuery(id+"F0.wireOp",EDGE,"E403"),sQuery(id+"F0.wireOp",EDGE,"E404"),sQuery(id+"F0.wireOp",EDGE,"E405"),sQuery(id+"F0.wireOp",EDGE,"E406"),sQuery(id+"F0.wireOp",EDGE,"E407"),sQuery(id+"F0.wireOp",EDGE,"E408"),sQuery(id+"F0.wireOp",EDGE,"E409"),sQuery(id+"F0.wireOp",EDGE,"E410"),sQuery(id+"F0.wireOp",EDGE,"E411"),sQuery(id+"F0.wireOp",EDGE,"E412"),sQuery(id+"F0.wireOp",EDGE,"E413"),sQuery(id+"F0.wireOp",EDGE,"E414"),sQuery(id+"F0.wireOp",EDGE,"E415"),sQuery(id+"F0.wireOp",EDGE,"E416"),sQuery(id+"F0.wireOp",EDGE,"E417"),sQuery(id+"F0.wireOp",EDGE,"E418"),sQuery(id+"F0.wireOp",EDGE,"E419"),sQuery(id+"F0.wireOp",EDGE,"E420"),sQuery(id+"F0.wireOp",EDGE,"E421"),sQuery(id+"F0.wireOp",EDGE,"E422"),sQuery(id+"F0.wireOp",EDGE,"E423"),sQuery(id+"F0.wireOp",EDGE,"E424"),sQuery(id+"F0.wireOp",EDGE,"E425"),sQuery(id+"F0.wireOp",EDGE,"E426"),sQuery(id+"F0.wireOp",EDGE,"E427"),sQuery(id+"F0.wireOp",EDGE,"E428"),sQuery(id+"F0.wireOp",EDGE,"E429"),sQuery(id+"F0.wireOp",EDGE,"E430"),sQuery(id+"F0.wireOp",EDGE,"E431"),sQuery(id+"F0.wireOp",EDGE,"E432"),sQuery(id+"F0.wireOp",EDGE,"E433"),sQuery(id+"F0.wireOp",EDGE,"E434"),sQuery(id+"F0.wireOp",EDGE,"E435"),sQuery(id+"F0.wireOp",EDGE,"E436"),sQuery(id+"F0.wireOp",EDGE,"E437"),sQuery(id+"F0.wireOp",EDGE,"E438"),sQuery(id+"F0.wireOp",EDGE,"E439"),sQuery(id+"F0.wireOp",EDGE,"E440"),sQuery(id+"F0.wireOp",EDGE,"E441"),sQuery(id+"F0.wireOp",EDGE,"E442"),sQuery(id+"F0.wireOp",EDGE,"E443"),sQuery(id+"F0.wireOp",EDGE,"E444"),sQuery(id+"F0.wireOp",EDGE,"E445"),sQuery(id+"F0.wireOp",EDGE,"E446"),sQuery(id+"F0.wireOp",EDGE,"E447"),sQuery(id+"F0.wireOp",EDGE,"E448"),sQuery(id+"F0.wireOp",EDGE,"E449"),sQuery(id+"F0.wireOp",EDGE,"E450"),sQuery(id+"F0.wireOp",EDGE,"E451"),sQuery(id+"F0.wireOp",EDGE,"E452"),sQuery(id+"F0.wireOp",EDGE,"E453"),sQuery(id+"F0.wireOp",EDGE,"E454"),sQuery(id+"F0.wireOp",EDGE,"E455"),sQuery(id+"F0.wireOp",EDGE,"E456"),sQuery(id+"F0.wireOp",EDGE,"E457"),sQuery(id+"F0.wireOp",EDGE,"E458"),sQuery(id+"F0.wireOp",EDGE,"E459"),sQuery(id+"F0.wireOp",EDGE,"E460"),sQuery(id+"F0.wireOp",EDGE,"E461"),sQuery(id+"F0.wireOp",EDGE,"E462"),sQuery(id+"F0.wireOp",EDGE,"E463"),sQuery(id+"F0.wireOp",EDGE,"E464"),sQuery(id+"F0.wireOp",EDGE,"E465"),sQuery(id+"F0.wireOp",EDGE,"E466"),sQuery(id+"F0.wireOp",EDGE,"E467"),sQuery(id+"F0.wireOp",EDGE,"E468"),sQuery(id+"F0.wireOp",EDGE,"E469"),sQuery(id+"F0.wireOp",EDGE,"E470"),sQuery(id+"F0.wireOp",EDGE,"E471"),sQuery(id+"F0.wireOp",EDGE,"E472"),sQuery(id+"F0.wireOp",EDGE,"E473"),sQuery(id+"F0.wireOp",EDGE,"E474"),sQuery(id+"F0.wireOp",EDGE,"E475"),sQuery(id+"F0.wireOp",EDGE,"E476"),sQuery(id+"F0.wireOp",EDGE,"E477"),sQuery(id+"F0.wireOp",EDGE,"E478"),sQuery(id+"F0.wireOp",EDGE,"E479"),sQuery(id+"F0.wireOp",EDGE,"E480"),sQuery(id+"F0.wireOp",EDGE,"E481"),sQuery(id+"F0.wireOp",EDGE,"E482"),sQuery(id+"F0.wireOp",EDGE,"E483"),sQuery(id+"F0.wireOp",EDGE,"E484"),sQuery(id+"F0.wireOp",EDGE,"E485"),sQuery(id+"F0.wireOp",EDGE,"E486"),sQuery(id+"F0.wireOp",EDGE,"E487"),sQuery(id+"F0.wireOp",EDGE,"E488"),sQuery(id+"F0.wireOp",EDGE,"E489"),sQuery(id+"F0.wireOp",EDGE,"E490"),sQuery(id+"F0.wireOp",EDGE,"E491"),sQuery(id+"F0.wireOp",EDGE,"E492"),sQuery(id+"F0.wireOp",EDGE,"E493"),sQuery(id+"F0.wireOp",EDGE,"E494"),sQuery(id+"F0.wireOp",EDGE,"E495"),sQuery(id+"F0.wireOp",EDGE,"E496"),sQuery(id+"F0.wireOp",EDGE,"E497"),sQuery(id+"F0.wireOp",EDGE,"E498"),sQuery(id+"F0.wireOp",EDGE,"E499"),sQuery(id+"F0.wireOp",EDGE,"E500"),sQuery(id+"F0.wireOp",EDGE,"E501"),sQuery(id+"F0.wireOp",EDGE,"E502"),sQuery(id+"F0.wireOp",EDGE,"E503"),sQuery(id+"F0.wireOp",EDGE,"E504"),sQuery(id+"F0.wireOp",EDGE,"E505"),sQuery(id+"F0.wireOp",EDGE,"E506"),sQuery(id+"F0.wireOp",EDGE,"E507"),sQuery(id+"F0.wireOp",EDGE,"E508"),sQuery(id+"F0.wireOp",EDGE,"E509"),sQuery(id+"F0.wireOp",EDGE,"E510"),sQuery(id+"F0.wireOp",EDGE,"E511"),sQuery(id+"F0.wireOp",EDGE,"E512"),sQuery(id+"F0.wireOp",EDGE,"E513"),sQuery(id+"F0.wireOp",EDGE,"E514"),sQuery(id+"F0.wireOp",EDGE,"E515"),sQuery(id+"F0.wireOp",EDGE,"E516"),sQuery(id+"F0.wireOp",EDGE,"E517"),sQuery(id+"F0.wireOp",EDGE,"E518"),sQuery(id+"F0.wireOp",EDGE,"E519"),sQuery(id+"F0.wireOp",EDGE,"E520"),sQuery(id+"F0.wireOp",EDGE,"E521"),sQuery(id+"F0.wireOp",EDGE,"E522"),sQuery(id+"F0.wireOp",EDGE,"E523"),sQuery(id+"F0.wireOp",EDGE,"E524"),sQuery(id+"F0.wireOp",EDGE,"E525"),sQuery(id+"F0.wireOp",EDGE,"E526"),sQuery(id+"F0.wireOp",EDGE,"E527"),sQuery(id+"F0.wireOp",EDGE,"E528"),sQuery(id+"F0.wireOp",EDGE,"E529"),sQuery(id+"F0.wireOp",EDGE,"E530"),sQuery(id+"F0.wireOp",EDGE,"E531"),sQuery(id+"F0.wireOp",EDGE,"E532"),sQuery(id+"F0.wireOp",EDGE,"E533"),sQuery(id+"F0.wireOp",EDGE,"E534"),sQuery(id+"F0.wireOp",EDGE,"E535"),sQuery(id+"F0.wireOp",EDGE,"E536"),sQuery(id+"F0.wireOp",EDGE,"E537"),sQuery(id+"F0.wireOp",EDGE,"E538"),sQuery(id+"F0.wireOp",EDGE,"E539"),sQuery(id+"F0.wireOp",EDGE,"E540"),sQuery(id+"F0.wireOp",EDGE,"E541"),sQuery(id+"F0.wireOp",EDGE,"E542"),sQuery(id+"F0.wireOp",EDGE,"E543"),sQuery(id+"F0.wireOp",EDGE,"E544"),sQuery(id+"F0.wireOp",EDGE,"E545"),sQuery(id+"F0.wireOp",EDGE,"E546"),sQuery(id+"F0.wireOp",EDGE,"E547"),sQuery(id+"F0.wireOp",EDGE,"E548"),sQuery(id+"F0.wireOp",EDGE,"E549"),sQuery(id+"F0.wireOp",EDGE,"E550"),sQuery(id+"F0.wireOp",EDGE,"E551"),sQuery(id+"F0.wireOp",EDGE,"E552"),sQuery(id+"F0.wireOp",EDGE,"E553"),sQuery(id+"F0.wireOp",EDGE,"E554"),sQuery(id+"F0.wireOp",EDGE,"E555"),sQuery(id+"F0.wireOp",EDGE,"E556"),sQuery(id+"F0.wireOp",EDGE,"E557"),sQuery(id+"F0.wireOp",EDGE,"E558"),sQuery(id+"F0.wireOp",EDGE,"E559"),sQuery(id+"F0.wireOp",EDGE,"E560"),sQuery(id+"F0.wireOp",EDGE,"E561"),sQuery(id+"F0.wireOp",EDGE,"E562"),sQuery(id+"F0.wireOp",EDGE,"E563"),sQuery(id+"F0.wireOp",EDGE,"E564"),sQuery(id+"F0.wireOp",EDGE,"E565"),sQuery(id+"F0.wireOp",EDGE,"E566"),sQuery(id+"F0.wireOp",EDGE,"E567"),sQuery(id+"F0.wireOp",EDGE,"E568"),sQuery(id+"F0.wireOp",EDGE,"E569"),sQuery(id+"F0.wireOp",EDGE,"E570"),sQuery(id+"F0.wireOp",EDGE,"E571"),sQuery(id+"F0.wireOp",EDGE,"E572"),sQuery(id+"F0.wireOp",EDGE,"E573"),sQuery(id+"F0.wireOp",EDGE,"E574"),sQuery(id+"F0.wireOp",EDGE,"E575")])],"isStart":false});
            fillet(context, id + "F4", {"entities" : qUnion([Q0, Q1]), "radius" : 2 * mm, "tangentPropagation" : true, "allowEdgeOverflow" : false});
        }
        {
            var Q0;
            Q0=makeQuery(id+"F1.opExtrude","CAP_FACE",FACE,{"disambiguationData":[OSD([sQuery(id+"F0.wireOp",EDGE,"E304"),sQuery(id+"F0.wireOp",EDGE,"E305"),sQuery(id+"F0.wireOp",EDGE,"E306"),sQuery(id+"F0.wireOp",EDGE,"E307"),sQuery(id+"F0.wireOp",EDGE,"E308"),sQuery(id+"F0.wireOp",EDGE,"E309"),sQuery(id+"F0.wireOp",EDGE,"E310"),sQuery(id+"F0.wireOp",EDGE,"E311"),sQuery(id+"F0.wireOp",EDGE,"E312"),sQuery(id+"F0.wireOp",EDGE,"E313"),sQuery(id+"F0.wireOp",EDGE,"E314"),sQuery(id+"F0.wireOp",EDGE,"E315"),sQuery(id+"F0.wireOp",EDGE,"E316"),sQuery(id+"F0.wireOp",EDGE,"E317"),sQuery(id+"F0.wireOp",EDGE,"E318"),sQuery(id+"F0.wireOp",EDGE,"E319"),sQuery(id+"F0.wireOp",EDGE,"E320"),sQuery(id+"F0.wireOp",EDGE,"E321"),sQuery(id+"F0.wireOp",EDGE,"E322"),sQuery(id+"F0.wireOp",EDGE,"E323"),sQuery(id+"F0.wireOp",EDGE,"E324"),sQuery(id+"F0.wireOp",EDGE,"E325"),sQuery(id+"F0.wireOp",EDGE,"E326"),sQuery(id+"F0.wireOp",EDGE,"E327"),sQuery(id+"F0.wireOp",EDGE,"E328"),sQuery(id+"F0.wireOp",EDGE,"E329"),sQuery(id+"F0.wireOp",EDGE,"E330"),sQuery(id+"F0.wireOp",EDGE,"E331"),sQuery(id+"F0.wireOp",EDGE,"E332"),sQuery(id+"F0.wireOp",EDGE,"E333"),sQuery(id+"F0.wireOp",EDGE,"E334"),sQuery(id+"F0.wireOp",EDGE,"E335"),sQuery(id+"F0.wireOp",EDGE,"E336"),sQuery(id+"F0.wireOp",EDGE,"E337"),sQuery(id+"F0.wireOp",EDGE,"E338"),sQuery(id+"F0.wireOp",EDGE,"E339"),sQuery(id+"F0.wireOp",EDGE,"E340"),sQuery(id+"F0.wireOp",EDGE,"E341"),sQuery(id+"F0.wireOp",EDGE,"E342"),sQuery(id+"F0.wireOp",EDGE,"E343"),sQuery(id+"F0.wireOp",EDGE,"E344"),sQuery(id+"F0.wireOp",EDGE,"E345"),sQuery(id+"F0.wireOp",EDGE,"E346"),sQuery(id+"F0.wireOp",EDGE,"E347"),sQuery(id+"F0.wireOp",EDGE,"E348"),sQuery(id+"F0.wireOp",EDGE,"E349"),sQuery(id+"F0.wireOp",EDGE,"E350"),sQuery(id+"F0.wireOp",EDGE,"E351"),sQuery(id+"F0.wireOp",EDGE,"E352"),sQuery(id+"F0.wireOp",EDGE,"E353"),sQuery(id+"F0.wireOp",EDGE,"E354"),sQuery(id+"F0.wireOp",EDGE,"E355"),sQuery(id+"F0.wireOp",EDGE,"E356"),sQuery(id+"F0.wireOp",EDGE,"E357"),sQuery(id+"F0.wireOp",EDGE,"E358"),sQuery(id+"F0.wireOp",EDGE,"E359"),sQuery(id+"F0.wireOp",EDGE,"E360"),sQuery(id+"F0.wireOp",EDGE,"E361"),sQuery(id+"F0.wireOp",EDGE,"E362"),sQuery(id+"F0.wireOp",EDGE,"E363"),sQuery(id+"F0.wireOp",EDGE,"E364"),sQuery(id+"F0.wireOp",EDGE,"E365"),sQuery(id+"F0.wireOp",EDGE,"E366"),sQuery(id+"F0.wireOp",EDGE,"E367"),sQuery(id+"F0.wireOp",EDGE,"E368"),sQuery(id+"F0.wireOp",EDGE,"E369"),sQuery(id+"F0.wireOp",EDGE,"E370"),sQuery(id+"F0.wireOp",EDGE,"E371"),sQuery(id+"F0.wireOp",EDGE,"E372"),sQuery(id+"F0.wireOp",EDGE,"E373"),sQuery(id+"F0.wireOp",EDGE,"E374"),sQuery(id+"F0.wireOp",EDGE,"E375"),sQuery(id+"F0.wireOp",EDGE,"E376"),sQuery(id+"F0.wireOp",EDGE,"E377"),sQuery(id+"F0.wireOp",EDGE,"E378"),sQuery(id+"F0.wireOp",EDGE,"E379"),sQuery(id+"F0.wireOp",EDGE,"E380"),sQuery(id+"F0.wireOp",EDGE,"E381"),sQuery(id+"F0.wireOp",EDGE,"E382"),sQuery(id+"F0.wireOp",EDGE,"E383"),sQuery(id+"F0.wireOp",EDGE,"E384"),sQuery(id+"F0.wireOp",EDGE,"E385"),sQuery(id+"F0.wireOp",EDGE,"E386"),sQuery(id+"F0.wireOp",EDGE,"E387"),sQuery(id+"F0.wireOp",EDGE,"E388"),sQuery(id+"F0.wireOp",EDGE,"E389"),sQuery(id+"F0.wireOp",EDGE,"E390"),sQuery(id+"F0.wireOp",EDGE,"E391"),sQuery(id+"F0.wireOp",EDGE,"E392"),sQuery(id+"F0.wireOp",EDGE,"E393"),sQuery(id+"F0.wireOp",EDGE,"E394"),sQuery(id+"F0.wireOp",EDGE,"E395"),sQuery(id+"F0.wireOp",EDGE,"E396"),sQuery(id+"F0.wireOp",EDGE,"E397"),sQuery(id+"F0.wireOp",EDGE,"E398"),sQuery(id+"F0.wireOp",EDGE,"E399"),sQuery(id+"F0.wireOp",EDGE,"E400"),sQuery(id+"F0.wireOp",EDGE,"E401"),sQuery(id+"F0.wireOp",EDGE,"E402"),sQuery(id+"F0.wireOp",EDGE,"E403"),sQuery(id+"F0.wireOp",EDGE,"E404"),sQuery(id+"F0.wireOp",EDGE,"E405"),sQuery(id+"F0.wireOp",EDGE,"E406"),sQuery(id+"F0.wireOp",EDGE,"E407"),sQuery(id+"F0.wireOp",EDGE,"E408"),sQuery(id+"F0.wireOp",EDGE,"E409"),sQuery(id+"F0.wireOp",EDGE,"E410"),sQuery(id+"F0.wireOp",EDGE,"E411"),sQuery(id+"F0.wireOp",EDGE,"E412"),sQuery(id+"F0.wireOp",EDGE,"E413"),sQuery(id+"F0.wireOp",EDGE,"E414"),sQuery(id+"F0.wireOp",EDGE,"E415"),sQuery(id+"F0.wireOp",EDGE,"E416"),sQuery(id+"F0.wireOp",EDGE,"E417"),sQuery(id+"F0.wireOp",EDGE,"E418"),sQuery(id+"F0.wireOp",EDGE,"E419"),sQuery(id+"F0.wireOp",EDGE,"E420"),sQuery(id+"F0.wireOp",EDGE,"E421"),sQuery(id+"F0.wireOp",EDGE,"E422"),sQuery(id+"F0.wireOp",EDGE,"E423"),sQuery(id+"F0.wireOp",EDGE,"E424"),sQuery(id+"F0.wireOp",EDGE,"E425"),sQuery(id+"F0.wireOp",EDGE,"E426"),sQuery(id+"F0.wireOp",EDGE,"E427"),sQuery(id+"F0.wireOp",EDGE,"E428"),sQuery(id+"F0.wireOp",EDGE,"E429"),sQuery(id+"F0.wireOp",EDGE,"E430"),sQuery(id+"F0.wireOp",EDGE,"E431"),sQuery(id+"F0.wireOp",EDGE,"E432"),sQuery(id+"F0.wireOp",EDGE,"E433"),sQuery(id+"F0.wireOp",EDGE,"E434"),sQuery(id+"F0.wireOp",EDGE,"E435"),sQuery(id+"F0.wireOp",EDGE,"E436"),sQuery(id+"F0.wireOp",EDGE,"E437"),sQuery(id+"F0.wireOp",EDGE,"E438"),sQuery(id+"F0.wireOp",EDGE,"E439"),sQuery(id+"F0.wireOp",EDGE,"E440"),sQuery(id+"F0.wireOp",EDGE,"E441"),sQuery(id+"F0.wireOp",EDGE,"E442"),sQuery(id+"F0.wireOp",EDGE,"E443"),sQuery(id+"F0.wireOp",EDGE,"E444"),sQuery(id+"F0.wireOp",EDGE,"E445"),sQuery(id+"F0.wireOp",EDGE,"E446"),sQuery(id+"F0.wireOp",EDGE,"E447"),sQuery(id+"F0.wireOp",EDGE,"E448"),sQuery(id+"F0.wireOp",EDGE,"E449"),sQuery(id+"F0.wireOp",EDGE,"E450"),sQuery(id+"F0.wireOp",EDGE,"E451"),sQuery(id+"F0.wireOp",EDGE,"E452"),sQuery(id+"F0.wireOp",EDGE,"E453"),sQuery(id+"F0.wireOp",EDGE,"E454"),sQuery(id+"F0.wireOp",EDGE,"E455"),sQuery(id+"F0.wireOp",EDGE,"E456"),sQuery(id+"F0.wireOp",EDGE,"E457"),sQuery(id+"F0.wireOp",EDGE,"E458"),sQuery(id+"F0.wireOp",EDGE,"E459"),sQuery(id+"F0.wireOp",EDGE,"E460"),sQuery(id+"F0.wireOp",EDGE,"E461"),sQuery(id+"F0.wireOp",EDGE,"E462"),sQuery(id+"F0.wireOp",EDGE,"E463"),sQuery(id+"F0.wireOp",EDGE,"E464"),sQuery(id+"F0.wireOp",EDGE,"E465"),sQuery(id+"F0.wireOp",EDGE,"E466"),sQuery(id+"F0.wireOp",EDGE,"E467"),sQuery(id+"F0.wireOp",EDGE,"E468"),sQuery(id+"F0.wireOp",EDGE,"E469"),sQuery(id+"F0.wireOp",EDGE,"E470"),sQuery(id+"F0.wireOp",EDGE,"E471"),sQuery(id+"F0.wireOp",EDGE,"E472"),sQuery(id+"F0.wireOp",EDGE,"E473"),sQuery(id+"F0.wireOp",EDGE,"E474"),sQuery(id+"F0.wireOp",EDGE,"E475"),sQuery(id+"F0.wireOp",EDGE,"E476"),sQuery(id+"F0.wireOp",EDGE,"E477"),sQuery(id+"F0.wireOp",EDGE,"E478"),sQuery(id+"F0.wireOp",EDGE,"E479"),sQuery(id+"F0.wireOp",EDGE,"E480"),sQuery(id+"F0.wireOp",EDGE,"E481"),sQuery(id+"F0.wireOp",EDGE,"E482"),sQuery(id+"F0.wireOp",EDGE,"E483"),sQuery(id+"F0.wireOp",EDGE,"E484"),sQuery(id+"F0.wireOp",EDGE,"E485"),sQuery(id+"F0.wireOp",EDGE,"E486"),sQuery(id+"F0.wireOp",EDGE,"E487"),sQuery(id+"F0.wireOp",EDGE,"E488"),sQuery(id+"F0.wireOp",EDGE,"E489"),sQuery(id+"F0.wireOp",EDGE,"E490"),sQuery(id+"F0.wireOp",EDGE,"E491"),sQuery(id+"F0.wireOp",EDGE,"E492"),sQuery(id+"F0.wireOp",EDGE,"E493"),sQuery(id+"F0.wireOp",EDGE,"E494"),sQuery(id+"F0.wireOp",EDGE,"E495"),sQuery(id+"F0.wireOp",EDGE,"E496"),sQuery(id+"F0.wireOp",EDGE,"E497"),sQuery(id+"F0.wireOp",EDGE,"E498"),sQuery(id+"F0.wireOp",EDGE,"E499"),sQuery(id+"F0.wireOp",EDGE,"E500"),sQuery(id+"F0.wireOp",EDGE,"E501"),sQuery(id+"F0.wireOp",EDGE,"E502"),sQuery(id+"F0.wireOp",EDGE,"E503"),sQuery(id+"F0.wireOp",EDGE,"E504"),sQuery(id+"F0.wireOp",EDGE,"E505"),sQuery(id+"F0.wireOp",EDGE,"E506"),sQuery(id+"F0.wireOp",EDGE,"E507"),sQuery(id+"F0.wireOp",EDGE,"E508"),sQuery(id+"F0.wireOp",EDGE,"E509"),sQuery(id+"F0.wireOp",EDGE,"E510"),sQuery(id+"F0.wireOp",EDGE,"E511"),sQuery(id+"F0.wireOp",EDGE,"E512"),sQuery(id+"F0.wireOp",EDGE,"E513"),sQuery(id+"F0.wireOp",EDGE,"E514"),sQuery(id+"F0.wireOp",EDGE,"E515"),sQuery(id+"F0.wireOp",EDGE,"E516"),sQuery(id+"F0.wireOp",EDGE,"E517"),sQuery(id+"F0.wireOp",EDGE,"E518"),sQuery(id+"F0.wireOp",EDGE,"E519"),sQuery(id+"F0.wireOp",EDGE,"E520"),sQuery(id+"F0.wireOp",EDGE,"E521"),sQuery(id+"F0.wireOp",EDGE,"E522"),sQuery(id+"F0.wireOp",EDGE,"E523"),sQuery(id+"F0.wireOp",EDGE,"E524"),sQuery(id+"F0.wireOp",EDGE,"E525"),sQuery(id+"F0.wireOp",EDGE,"E526"),sQuery(id+"F0.wireOp",EDGE,"E527"),sQuery(id+"F0.wireOp",EDGE,"E528"),sQuery(id+"F0.wireOp",EDGE,"E529"),sQuery(id+"F0.wireOp",EDGE,"E530"),sQuery(id+"F0.wireOp",EDGE,"E531"),sQuery(id+"F0.wireOp",EDGE,"E532"),sQuery(id+"F0.wireOp",EDGE,"E533"),sQuery(id+"F0.wireOp",EDGE,"E534"),sQuery(id+"F0.wireOp",EDGE,"E535"),sQuery(id+"F0.wireOp",EDGE,"E536"),sQuery(id+"F0.wireOp",EDGE,"E537"),sQuery(id+"F0.wireOp",EDGE,"E538"),sQuery(id+"F0.wireOp",EDGE,"E539"),sQuery(id+"F0.wireOp",EDGE,"E540"),sQuery(id+"F0.wireOp",EDGE,"E541"),sQuery(id+"F0.wireOp",EDGE,"E542"),sQuery(id+"F0.wireOp",EDGE,"E543"),sQuery(id+"F0.wireOp",EDGE,"E544"),sQuery(id+"F0.wireOp",EDGE,"E545"),sQuery(id+"F0.wireOp",EDGE,"E546"),sQuery(id+"F0.wireOp",EDGE,"E547"),sQuery(id+"F0.wireOp",EDGE,"E548"),sQuery(id+"F0.wireOp",EDGE,"E549"),sQuery(id+"F0.wireOp",EDGE,"E550"),sQuery(id+"F0.wireOp",EDGE,"E551"),sQuery(id+"F0.wireOp",EDGE,"E552"),sQuery(id+"F0.wireOp",EDGE,"E553"),sQuery(id+"F0.wireOp",EDGE,"E554"),sQuery(id+"F0.wireOp",EDGE,"E555"),sQuery(id+"F0.wireOp",EDGE,"E556"),sQuery(id+"F0.wireOp",EDGE,"E557"),sQuery(id+"F0.wireOp",EDGE,"E558"),sQuery(id+"F0.wireOp",EDGE,"E559"),sQuery(id+"F0.wireOp",EDGE,"E560"),sQuery(id+"F0.wireOp",EDGE,"E561"),sQuery(id+"F0.wireOp",EDGE,"E562"),sQuery(id+"F0.wireOp",EDGE,"E563"),sQuery(id+"F0.wireOp",EDGE,"E564"),sQuery(id+"F0.wireOp",EDGE,"E565"),sQuery(id+"F0.wireOp",EDGE,"E566"),sQuery(id+"F0.wireOp",EDGE,"E567"),sQuery(id+"F0.wireOp",EDGE,"E568"),sQuery(id+"F0.wireOp",EDGE,"E569"),sQuery(id+"F0.wireOp",EDGE,"E570"),sQuery(id+"F0.wireOp",EDGE,"E571"),sQuery(id+"F0.wireOp",EDGE,"E572"),sQuery(id+"F0.wireOp",EDGE,"E573"),sQuery(id+"F0.wireOp",EDGE,"E574"),sQuery(id+"F0.wireOp",EDGE,"E575")])],"isStart":false});
            var sketch = newSketch(context, id + "F5", { "sketchPlane" : qUnion([Q0])});
            skLineSegment(sketch, "E579", {"start": v(237.08, 420.97) * mm, "end": v(-348.53, -597.18) * mm});
            skLineSegment(sketch, "E580", {"start": v(-348.53, -597.18) * mm, "end": v(-348.53, -597.18) * mm});
            skLineSegment(sketch, "E581", {"start": v(-348.53, -597.18) * mm, "end": v(235.93, 418.98) * mm});
            skLineSegment(sketch, "E582", {"start": v(235.93, 418.98) * mm, "end": v(237.08, 420.97) * mm});
            skSolve(sketch);
        }
        {
            var Q0;
            Q0 = qSketchRegion(id + "F5", true);
            extrude(context, id + "F6", {"entities" : qUnion([Q0]), "operationType" : NewBodyOperationType.REMOVE, "oppositeDirection" : true, "depth" : 600 * mm, "offsetDistance" : 25 * mm});
        }
        {
            var Q0;
            {var subQ0=sQuery(id+"F0.wireOp",EDGE,"E96");var subQ1=sQuery(id+"F0.wireOp",EDGE,"E295");var subQ2=sQuery(id+"F0.wireOp",EDGE,"E95");var subQ3=sQuery(id+"F0.wireOp",EDGE,"E94");var subQ4=sQuery(id+"F0.wireOp",EDGE,"E93");var subQ5=sQuery(id+"F0.wireOp",EDGE,"E92");var subQ6=sQuery(id+"F0.wireOp",EDGE,"E91");var subQ7=sQuery(id+"F0.wireOp",EDGE,"E90");var subQ8=sQuery(id+"F0.wireOp",EDGE,"E89");var subQ9=sQuery(id+"F0.wireOp",EDGE,"E88");var subQ10=sQuery(id+"F0.wireOp",EDGE,"E87");var subQ11=sQuery(id+"F0.wireOp",EDGE,"E86");var subQ12=sQuery(id+"F0.wireOp",EDGE,"E85");var subQ13=sQuery(id+"F0.wireOp",EDGE,"E84");var subQ14=sQuery(id+"F0.wireOp",EDGE,"E83");var subQ15=sQuery(id+"F0.wireOp",EDGE,"E82");var subQ16=sQuery(id+"F0.wireOp",EDGE,"E81");var subQ17=sQuery(id+"F0.wireOp",EDGE,"E80");var subQ18=sQuery(id+"F0.wireOp",EDGE,"E79");var subQ19=sQuery(id+"F0.wireOp",EDGE,"E78");var subQ20=sQuery(id+"F0.wireOp",EDGE,"E77");var subQ21=sQuery(id+"F0.wireOp",EDGE,"E76");var subQ22=sQuery(id+"F0.wireOp",EDGE,"E75");var subQ23=sQuery(id+"F0.wireOp",EDGE,"E74");var subQ24=sQuery(id+"F0.wireOp",EDGE,"E73");var subQ25=sQuery(id+"F0.wireOp",EDGE,"E72");var subQ26=sQuery(id+"F0.wireOp",EDGE,"E71");var subQ27=sQuery(id+"F0.wireOp",EDGE,"E70");var subQ28=sQuery(id+"F0.wireOp",EDGE,"E69");var subQ29=sQuery(id+"F0.wireOp",EDGE,"E68");var subQ30=sQuery(id+"F0.wireOp",EDGE,"E67");var subQ31=sQuery(id+"F0.wireOp",EDGE,"E66");var subQ32=sQuery(id+"F0.wireOp",EDGE,"E65");var subQ33=sQuery(id+"F0.wireOp",EDGE,"E64");var subQ34=sQuery(id+"F0.wireOp",EDGE,"E63");var subQ35=sQuery(id+"F0.wireOp",EDGE,"E62");var subQ36=sQuery(id+"F0.wireOp",EDGE,"E61");var subQ37=sQuery(id+"F0.wireOp",EDGE,"E60");var subQ38=sQuery(id+"F0.wireOp",EDGE,"E59");var subQ39=sQuery(id+"F0.wireOp",EDGE,"E58");var subQ40=sQuery(id+"F0.wireOp",EDGE,"E57");var subQ41=sQuery(id+"F0.wireOp",EDGE,"E56");var subQ42=sQuery(id+"F0.wireOp",EDGE,"E55");var subQ43=sQuery(id+"F0.wireOp",EDGE,"E54");var subQ44=sQuery(id+"F0.wireOp",EDGE,"E53");var subQ45=sQuery(id+"F0.wireOp",EDGE,"E52");var subQ46=sQuery(id+"F0.wireOp",EDGE,"E51");var subQ47=sQuery(id+"F0.wireOp",EDGE,"E50");var subQ48=sQuery(id+"F0.wireOp",EDGE,"E49");var subQ49=sQuery(id+"F0.wireOp",EDGE,"E48");var subQ50=sQuery(id+"F0.wireOp",EDGE,"E47");var subQ51=sQuery(id+"F0.wireOp",EDGE,"E22");var subQ52=sQuery(id+"F0.wireOp",EDGE,"E21");var subQ53=sQuery(id+"F0.wireOp",EDGE,"E20");var subQ54=sQuery(id+"F0.wireOp",EDGE,"E19");var subQ55=sQuery(id+"F0.wireOp",EDGE,"E18");var subQ56=sQuery(id+"F0.wireOp",EDGE,"E17");var subQ57=sQuery(id+"F0.wireOp",EDGE,"E16");var subQ58=sQuery(id+"F0.wireOp",EDGE,"E15");var subQ59=sQuery(id+"F0.wireOp",EDGE,"E14");var subQ60=sQuery(id+"F0.wireOp",EDGE,"E13");var subQ61=sQuery(id+"F0.wireOp",EDGE,"E12");var subQ62=sQuery(id+"F0.wireOp",EDGE,"E11");var subQ63=sQuery(id+"F0.wireOp",EDGE,"E4");var subQ64=sQuery(id+"F0.wireOp",EDGE,"E3");var subQ65=sQuery(id+"F0.wireOp",EDGE,"E2");var subQ66=sQuery(id+"F0.wireOp",EDGE,"E1");var subQ67=sQuery(id+"F0.wireOp",EDGE,"E0");var subQ68=sQuery(id+"F0.wireOp",EDGE,"E5");var subQ69=sQuery(id+"F0.wireOp",EDGE,"E6");var subQ70=sQuery(id+"F0.wireOp",EDGE,"E7");var subQ71=sQuery(id+"F0.wireOp",EDGE,"E8");var subQ72=sQuery(id+"F0.wireOp",EDGE,"E9");var subQ73=sQuery(id+"F0.wireOp",EDGE,"E10");var subQ74=sQuery(id+"F0.wireOp",EDGE,"E23");var subQ75=sQuery(id+"F0.wireOp",EDGE,"E24");var subQ76=sQuery(id+"F0.wireOp",EDGE,"E25");var subQ77=sQuery(id+"F0.wireOp",EDGE,"E26");var subQ78=sQuery(id+"F0.wireOp",EDGE,"E27");var subQ79=sQuery(id+"F0.wireOp",EDGE,"E28");var subQ80=sQuery(id+"F0.wireOp",EDGE,"E29");var subQ81=sQuery(id+"F0.wireOp",EDGE,"E30");var subQ82=sQuery(id+"F0.wireOp",EDGE,"E31");var subQ83=sQuery(id+"F0.wireOp",EDGE,"E32");var subQ84=sQuery(id+"F0.wireOp",EDGE,"E33");var subQ85=sQuery(id+"F0.wireOp",EDGE,"E34");var subQ86=sQuery(id+"F0.wireOp",EDGE,"E35");var subQ87=sQuery(id+"F0.wireOp",EDGE,"E36");var subQ88=sQuery(id+"F0.wireOp",EDGE,"E37");var subQ89=sQuery(id+"F0.wireOp",EDGE,"E38");var subQ90=sQuery(id+"F0.wireOp",EDGE,"E39");var subQ91=sQuery(id+"F0.wireOp",EDGE,"E40");var subQ92=sQuery(id+"F0.wireOp",EDGE,"E41");var subQ93=sQuery(id+"F0.wireOp",EDGE,"E42");var subQ94=sQuery(id+"F0.wireOp",EDGE,"E43");var subQ95=sQuery(id+"F0.wireOp",EDGE,"E44");var subQ96=sQuery(id+"F0.wireOp",EDGE,"E45");var subQ97=sQuery(id+"F0.wireOp",EDGE,"E46");var subQ98=sQuery(id+"F0.wireOp",EDGE,"E97");var subQ99=sQuery(id+"F0.wireOp",EDGE,"E296");var subQ100=sQuery(id+"F0.wireOp",EDGE,"E98");var subQ101=sQuery(id+"F0.wireOp",EDGE,"E297");var subQ102=sQuery(id+"F0.wireOp",EDGE,"E99");var subQ103=sQuery(id+"F0.wireOp",EDGE,"E298");var subQ104=sQuery(id+"F0.wireOp",EDGE,"E100");var subQ105=sQuery(id+"F0.wireOp",EDGE,"E299");var subQ106=sQuery(id+"F0.wireOp",EDGE,"E101");var subQ107=sQuery(id+"F0.wireOp",EDGE,"E300");var subQ108=sQuery(id+"F0.wireOp",EDGE,"E102");var subQ109=sQuery(id+"F0.wireOp",EDGE,"E301");var subQ110=sQuery(id+"F0.wireOp",EDGE,"E103");var subQ111=sQuery(id+"F0.wireOp",EDGE,"E302");var subQ112=sQuery(id+"F0.wireOp",EDGE,"E104");var subQ113=sQuery(id+"F0.wireOp",EDGE,"E303");var subQ114=sQuery(id+"F0.wireOp",EDGE,"E105");var subQ115=sQuery(id+"F0.wireOp",EDGE,"E106");var subQ116=sQuery(id+"F0.wireOp",EDGE,"E107");var subQ117=sQuery(id+"F0.wireOp",EDGE,"E108");var subQ118=sQuery(id+"F0.wireOp",EDGE,"E109");var subQ119=sQuery(id+"F0.wireOp",EDGE,"E110");var subQ120=sQuery(id+"F0.wireOp",EDGE,"E111");var subQ121=sQuery(id+"F0.wireOp",EDGE,"E112");var subQ122=sQuery(id+"F0.wireOp",EDGE,"E113");var subQ123=sQuery(id+"F0.wireOp",EDGE,"E114");var subQ124=sQuery(id+"F0.wireOp",EDGE,"E115");var subQ125=sQuery(id+"F0.wireOp",EDGE,"E116");var subQ126=sQuery(id+"F0.wireOp",EDGE,"E117");var subQ127=sQuery(id+"F0.wireOp",EDGE,"E118");var subQ128=sQuery(id+"F0.wireOp",EDGE,"E119");var subQ129=sQuery(id+"F0.wireOp",EDGE,"E120");var subQ130=sQuery(id+"F0.wireOp",EDGE,"E121");var subQ131=sQuery(id+"F0.wireOp",EDGE,"E122");var subQ132=sQuery(id+"F0.wireOp",EDGE,"E123");var subQ133=sQuery(id+"F0.wireOp",EDGE,"E124");var subQ134=sQuery(id+"F0.wireOp",EDGE,"E125");var subQ135=sQuery(id+"F0.wireOp",EDGE,"E126");var subQ136=sQuery(id+"F0.wireOp",EDGE,"E127");var subQ137=sQuery(id+"F0.wireOp",EDGE,"E128");var subQ138=sQuery(id+"F0.wireOp",EDGE,"E129");var subQ139=sQuery(id+"F0.wireOp",EDGE,"E130");var subQ140=sQuery(id+"F0.wireOp",EDGE,"E131");var subQ141=sQuery(id+"F0.wireOp",EDGE,"E132");var subQ142=sQuery(id+"F0.wireOp",EDGE,"E133");var subQ143=sQuery(id+"F0.wireOp",EDGE,"E134");var subQ144=sQuery(id+"F0.wireOp",EDGE,"E135");var subQ145=sQuery(id+"F0.wireOp",EDGE,"E136");var subQ146=sQuery(id+"F0.wireOp",EDGE,"E137");var subQ147=sQuery(id+"F0.wireOp",EDGE,"E138");var subQ148=sQuery(id+"F0.wireOp",EDGE,"E139");var subQ149=sQuery(id+"F0.wireOp",EDGE,"E140");var subQ150=sQuery(id+"F0.wireOp",EDGE,"E141");var subQ151=sQuery(id+"F0.wireOp",EDGE,"E142");var subQ152=sQuery(id+"F0.wireOp",EDGE,"E143");var subQ153=sQuery(id+"F0.wireOp",EDGE,"E144");var subQ154=sQuery(id+"F0.wireOp",EDGE,"E145");var subQ155=sQuery(id+"F0.wireOp",EDGE,"E146");var subQ156=sQuery(id+"F0.wireOp",EDGE,"E147");var subQ157=sQuery(id+"F0.wireOp",EDGE,"E148");var subQ158=sQuery(id+"F0.wireOp",EDGE,"E149");var subQ159=sQuery(id+"F0.wireOp",EDGE,"E150");var subQ160=sQuery(id+"F0.wireOp",EDGE,"E151");Q0=makeQuery(id+"F6.boolean.opBoolean","SPLIT",FACE,{"disambiguationData":[TD([makeQuery(id+"F4.opFillet","BLEND_FACE",FACE,{"disambiguationData":[OSD([subQ67])]})])],"derivedFrom":makeQuery(id+"F1.opExtrude","CAP_FACE",FACE,{"disambiguationData":[OSD([subQ67,subQ66,subQ65,subQ64,subQ63,subQ68,subQ69,subQ70,subQ71,subQ72,subQ73,subQ62,subQ61,subQ60,subQ59,subQ58,subQ57,subQ56,subQ55,subQ54,subQ53,subQ52,subQ51,subQ74,subQ75,subQ76,subQ77,subQ78,subQ79,subQ80,subQ81,subQ82,subQ83,subQ84,subQ85,subQ86,subQ87,subQ88,subQ89,subQ90,subQ91,subQ92,subQ93,subQ94,subQ95,subQ96,subQ97,subQ50,subQ49,subQ48,subQ47,subQ46,subQ45,subQ44,subQ43,subQ42,subQ41,subQ40,subQ39,subQ38,subQ37,subQ36,subQ35,subQ34,subQ33,subQ32,subQ31,subQ30,subQ29,subQ28,subQ27,subQ26,subQ25,subQ24,subQ23,subQ22,subQ21,subQ20,subQ19,subQ18,subQ17,subQ16,subQ15,subQ14,subQ13,subQ12,subQ11,subQ10,subQ9,subQ8,subQ7,subQ6,subQ5,subQ4,subQ3,subQ2,subQ0,subQ98,subQ100,subQ102,subQ104,subQ106,subQ108,subQ110,subQ112,subQ114,subQ115,subQ116,subQ117,subQ118,subQ119,subQ120,subQ121,subQ122,subQ123,subQ124,subQ125,subQ126,subQ127,subQ128,subQ129,subQ130,subQ131,subQ132,subQ133,subQ134,subQ135,subQ136,subQ137,subQ138,subQ139,subQ140,subQ141,subQ142,subQ143,subQ144,subQ145,subQ146,subQ147,subQ148,subQ149,subQ150,subQ151,subQ152,subQ153,subQ154,subQ155,subQ156,subQ157,subQ158,subQ159,subQ160,sQuery(id+"F0.wireOp",EDGE,"E152"),sQuery(id+"F0.wireOp",EDGE,"E153"),sQuery(id+"F0.wireOp",EDGE,"E154"),sQuery(id+"F0.wireOp",EDGE,"E155"),sQuery(id+"F0.wireOp",EDGE,"E156"),sQuery(id+"F0.wireOp",EDGE,"E157"),sQuery(id+"F0.wireOp",EDGE,"E158"),sQuery(id+"F0.wireOp",EDGE,"E159"),sQuery(id+"F0.wireOp",EDGE,"E160"),sQuery(id+"F0.wireOp",EDGE,"E161"),sQuery(id+"F0.wireOp",EDGE,"E162"),sQuery(id+"F0.wireOp",EDGE,"E163"),sQuery(id+"F0.wireOp",EDGE,"E164"),sQuery(id+"F0.wireOp",EDGE,"E165"),sQuery(id+"F0.wireOp",EDGE,"E166"),sQuery(id+"F0.wireOp",EDGE,"E167"),sQuery(id+"F0.wireOp",EDGE,"E168"),sQuery(id+"F0.wireOp",EDGE,"E169"),sQuery(id+"F0.wireOp",EDGE,"E170"),sQuery(id+"F0.wireOp",EDGE,"E171"),sQuery(id+"F0.wireOp",EDGE,"E172"),sQuery(id+"F0.wireOp",EDGE,"E173"),sQuery(id+"F0.wireOp",EDGE,"E174"),sQuery(id+"F0.wireOp",EDGE,"E175"),sQuery(id+"F0.wireOp",EDGE,"E176"),sQuery(id+"F0.wireOp",EDGE,"E177"),sQuery(id+"F0.wireOp",EDGE,"E178"),sQuery(id+"F0.wireOp",EDGE,"E179"),sQuery(id+"F0.wireOp",EDGE,"E180"),sQuery(id+"F0.wireOp",EDGE,"E181"),sQuery(id+"F0.wireOp",EDGE,"E182"),sQuery(id+"F0.wireOp",EDGE,"E183"),sQuery(id+"F0.wireOp",EDGE,"E184"),sQuery(id+"F0.wireOp",EDGE,"E185"),sQuery(id+"F0.wireOp",EDGE,"E186"),sQuery(id+"F0.wireOp",EDGE,"E187"),sQuery(id+"F0.wireOp",EDGE,"E188"),sQuery(id+"F0.wireOp",EDGE,"E189"),sQuery(id+"F0.wireOp",EDGE,"E190"),sQuery(id+"F0.wireOp",EDGE,"E191"),sQuery(id+"F0.wireOp",EDGE,"E192"),sQuery(id+"F0.wireOp",EDGE,"E193"),sQuery(id+"F0.wireOp",EDGE,"E194"),sQuery(id+"F0.wireOp",EDGE,"E195"),sQuery(id+"F0.wireOp",EDGE,"E196"),sQuery(id+"F0.wireOp",EDGE,"E197"),sQuery(id+"F0.wireOp",EDGE,"E198"),sQuery(id+"F0.wireOp",EDGE,"E199"),sQuery(id+"F0.wireOp",EDGE,"E200"),sQuery(id+"F0.wireOp",EDGE,"E201"),sQuery(id+"F0.wireOp",EDGE,"E202"),sQuery(id+"F0.wireOp",EDGE,"E203"),sQuery(id+"F0.wireOp",EDGE,"E204"),sQuery(id+"F0.wireOp",EDGE,"E205"),sQuery(id+"F0.wireOp",EDGE,"E206"),sQuery(id+"F0.wireOp",EDGE,"E207"),sQuery(id+"F0.wireOp",EDGE,"E208"),sQuery(id+"F0.wireOp",EDGE,"E209"),sQuery(id+"F0.wireOp",EDGE,"E210"),sQuery(id+"F0.wireOp",EDGE,"E211"),sQuery(id+"F0.wireOp",EDGE,"E212"),sQuery(id+"F0.wireOp",EDGE,"E213"),sQuery(id+"F0.wireOp",EDGE,"E214"),sQuery(id+"F0.wireOp",EDGE,"E215"),sQuery(id+"F0.wireOp",EDGE,"E216"),sQuery(id+"F0.wireOp",EDGE,"E217"),sQuery(id+"F0.wireOp",EDGE,"E218"),sQuery(id+"F0.wireOp",EDGE,"E219"),sQuery(id+"F0.wireOp",EDGE,"E220"),sQuery(id+"F0.wireOp",EDGE,"E221"),sQuery(id+"F0.wireOp",EDGE,"E222"),sQuery(id+"F0.wireOp",EDGE,"E223"),sQuery(id+"F0.wireOp",EDGE,"E224"),sQuery(id+"F0.wireOp",EDGE,"E225"),sQuery(id+"F0.wireOp",EDGE,"E226"),sQuery(id+"F0.wireOp",EDGE,"E227"),sQuery(id+"F0.wireOp",EDGE,"E228"),sQuery(id+"F0.wireOp",EDGE,"E229"),sQuery(id+"F0.wireOp",EDGE,"E230"),sQuery(id+"F0.wireOp",EDGE,"E231"),sQuery(id+"F0.wireOp",EDGE,"E232"),sQuery(id+"F0.wireOp",EDGE,"E233"),sQuery(id+"F0.wireOp",EDGE,"E234"),sQuery(id+"F0.wireOp",EDGE,"E235"),sQuery(id+"F0.wireOp",EDGE,"E236"),sQuery(id+"F0.wireOp",EDGE,"E237"),sQuery(id+"F0.wireOp",EDGE,"E238"),sQuery(id+"F0.wireOp",EDGE,"E239"),sQuery(id+"F0.wireOp",EDGE,"E240"),sQuery(id+"F0.wireOp",EDGE,"E241"),sQuery(id+"F0.wireOp",EDGE,"E242"),sQuery(id+"F0.wireOp",EDGE,"E243"),sQuery(id+"F0.wireOp",EDGE,"E244"),sQuery(id+"F0.wireOp",EDGE,"E245"),sQuery(id+"F0.wireOp",EDGE,"E246"),sQuery(id+"F0.wireOp",EDGE,"E247"),sQuery(id+"F0.wireOp",EDGE,"E248"),sQuery(id+"F0.wireOp",EDGE,"E249"),sQuery(id+"F0.wireOp",EDGE,"E250"),sQuery(id+"F0.wireOp",EDGE,"E251"),sQuery(id+"F0.wireOp",EDGE,"E252"),sQuery(id+"F0.wireOp",EDGE,"E253"),sQuery(id+"F0.wireOp",EDGE,"E254"),sQuery(id+"F0.wireOp",EDGE,"E255"),sQuery(id+"F0.wireOp",EDGE,"E256"),sQuery(id+"F0.wireOp",EDGE,"E257"),sQuery(id+"F0.wireOp",EDGE,"E258"),sQuery(id+"F0.wireOp",EDGE,"E259"),sQuery(id+"F0.wireOp",EDGE,"E260"),sQuery(id+"F0.wireOp",EDGE,"E261"),sQuery(id+"F0.wireOp",EDGE,"E262"),sQuery(id+"F0.wireOp",EDGE,"E263"),sQuery(id+"F0.wireOp",EDGE,"E264"),sQuery(id+"F0.wireOp",EDGE,"E265"),sQuery(id+"F0.wireOp",EDGE,"E266"),sQuery(id+"F0.wireOp",EDGE,"E267"),sQuery(id+"F0.wireOp",EDGE,"E268"),sQuery(id+"F0.wireOp",EDGE,"E269"),sQuery(id+"F0.wireOp",EDGE,"E270"),sQuery(id+"F0.wireOp",EDGE,"E271"),sQuery(id+"F0.wireOp",EDGE,"E272"),sQuery(id+"F0.wireOp",EDGE,"E273"),sQuery(id+"F0.wireOp",EDGE,"E274"),sQuery(id+"F0.wireOp",EDGE,"E275"),sQuery(id+"F0.wireOp",EDGE,"E276"),sQuery(id+"F0.wireOp",EDGE,"E277"),sQuery(id+"F0.wireOp",EDGE,"E278"),sQuery(id+"F0.wireOp",EDGE,"E279"),sQuery(id+"F0.wireOp",EDGE,"E280"),sQuery(id+"F0.wireOp",EDGE,"E281"),sQuery(id+"F0.wireOp",EDGE,"E282"),sQuery(id+"F0.wireOp",EDGE,"E283"),sQuery(id+"F0.wireOp",EDGE,"E284"),sQuery(id+"F0.wireOp",EDGE,"E285"),sQuery(id+"F0.wireOp",EDGE,"E286"),sQuery(id+"F0.wireOp",EDGE,"E287"),sQuery(id+"F0.wireOp",EDGE,"E288"),sQuery(id+"F0.wireOp",EDGE,"E289"),sQuery(id+"F0.wireOp",EDGE,"E290"),sQuery(id+"F0.wireOp",EDGE,"E291"),sQuery(id+"F0.wireOp",EDGE,"E292"),sQuery(id+"F0.wireOp",EDGE,"E293"),sQuery(id+"F0.wireOp",EDGE,"E294"),subQ1,subQ99,subQ101,subQ103,subQ105,subQ107,subQ109,subQ111,subQ113])],"isStart":false})});}
            var sketch = newSketch(context, id + "F7", { "sketchPlane" : qUnion([Q0])});
            skLineSegment(sketch, "E583", {"start": v(-113.74, -150.74) * mm, "end": v(579.77, -483.9) * mm});
            skLineSegment(sketch, "E584", {"start": v(579.77, -483.9) * mm, "end": v(579.77, -483.9) * mm});
            skLineSegment(sketch, "E585", {"start": v(579.77, -483.9) * mm, "end": v(-111.94, -151.62) * mm});
            skLineSegment(sketch, "E586", {"start": v(-111.94, -151.62) * mm, "end": v(-113.74, -150.74) * mm});
            skSolve(sketch);
        }
        {
            var Q0;
            Q0 = qSketchRegion(id + "F7", true);
            extrude(context, id + "F8", {"entities" : qUnion([Q0]), "operationType" : NewBodyOperationType.REMOVE, "oppositeDirection" : true, "depth" : 388 * mm, "offsetDistance" : 25 * mm});
        }
    });
